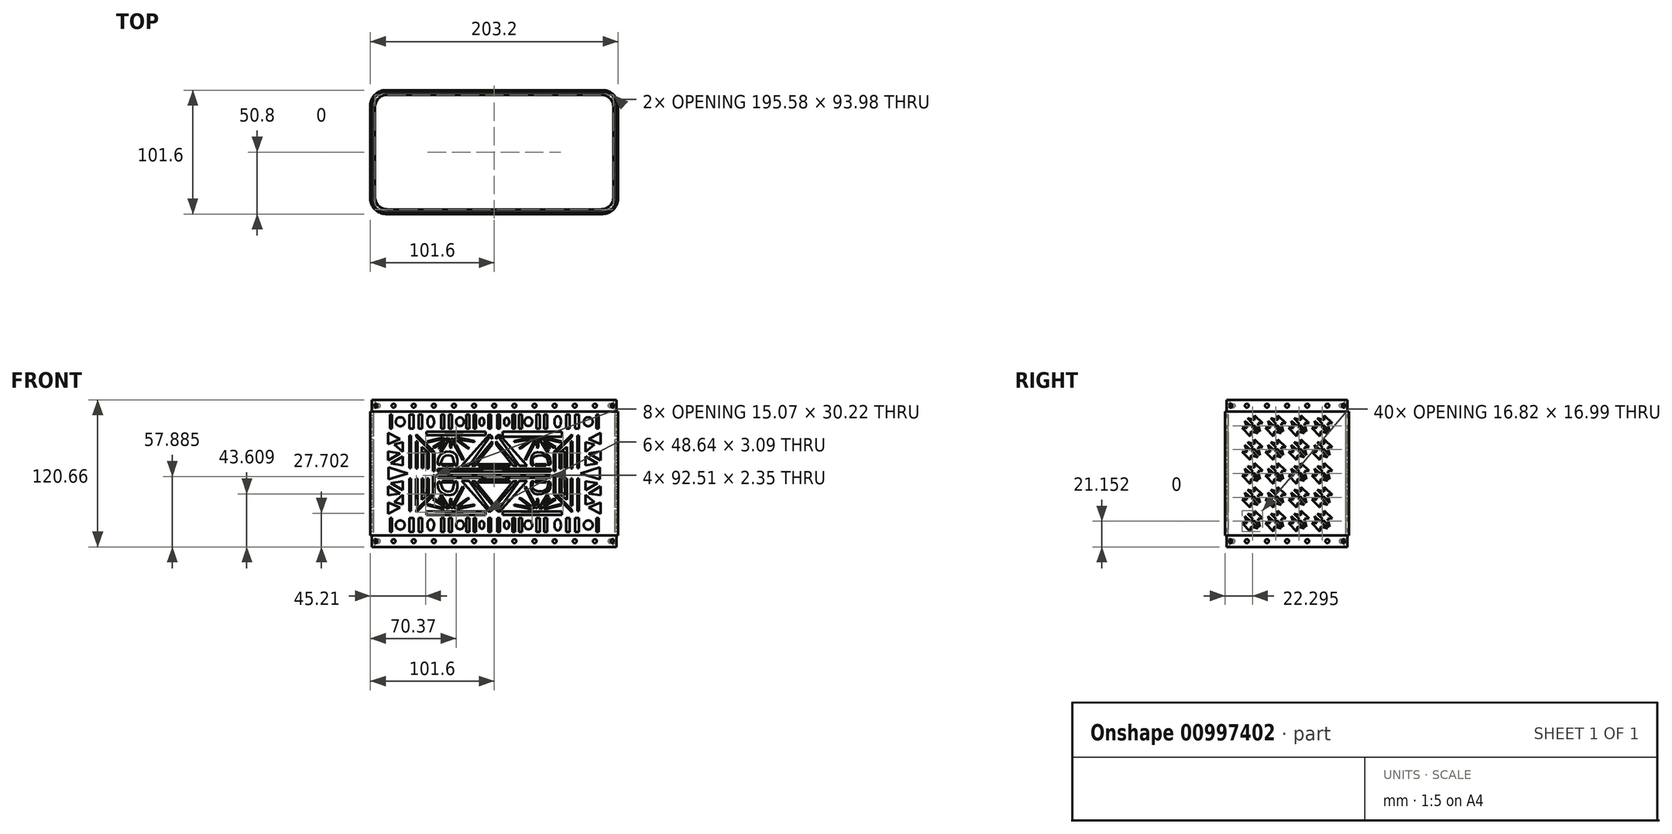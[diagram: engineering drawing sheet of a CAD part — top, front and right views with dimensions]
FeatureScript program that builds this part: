
annotation { "Feature Type Name" : "Feature", "Feature Type Description" : "" }
export const myFeature = defineFeature(function(context is Context, id is Id, definition is map)
    precondition{}
    {
        {
            var Q0;
            Q0=qCreatedBy(makeId("Top.planeOp"),FACE);
            var sketch = newSketch(context, id + "F0", { "sketchPlane" : qUnion([Q0])});
            skLineSegment(sketch, "E0.bottom", {"start": v(-88.9, 50.8) * mm, "end": v(88.9, 50.8) * mm});
            skLineSegment(sketch, "E0.top", {"start": v(-88.9, -50.8) * mm, "end": v(88.9, -50.8) * mm});
            skLineSegment(sketch, "E0.left", {"start": v(-101.6, 38.1) * mm, "end": v(-101.6, -38.1) * mm});
            skLineSegment(sketch, "E0.right", {"start": v(101.6, 38.1) * mm, "end": v(101.6, -38.1) * mm});
            skPoint(sketch, "E1.visualSharp", {"position": v(-101.6, -50.8) * mm});
            skArc(sketch, "E1.filletArc", {"start": v(-101.6, -38.1) * mm, "mid": v(-97.88, -47.08) * mm, "end": v(-88.9, -50.8) * mm});
            skPoint(sketch, "E2.visualSharp", {"position": v(101.6, -50.8) * mm});
            skArc(sketch, "E2.filletArc", {"start": v(88.9, -50.8) * mm, "mid": v(97.88, -47.08) * mm, "end": v(101.6, -38.1) * mm});
            skPoint(sketch, "E3.visualSharp", {"position": v(-101.6, 50.8) * mm});
            skArc(sketch, "E3.filletArc", {"start": v(-88.9, 50.8) * mm, "mid": v(-97.88, 47.08) * mm, "end": v(-101.6, 38.1) * mm});
            skPoint(sketch, "E4.visualSharp", {"position": v(101.6, 50.8) * mm});
            skArc(sketch, "E4.filletArc", {"start": v(101.6, 38.1) * mm, "mid": v(97.88, 47.08) * mm, "end": v(88.9, 50.8) * mm});
            skSolve(sketch);
        }
        {
            var Q0;
            Q0=makeQuery(id+"F0.imprint","IMPRINT",FACE,{"disambiguationData":[TD([[makeQuery(id+"F0.imprint","IMPRINT",EDGE,{"derivedFrom":sQuery(id+"F0.wireOp",EDGE,"E0.bottom")}),-1.0]])]});
            extrude(context, id + "F1", {"entities" : qUnion([Q0]), "depth" : 101.6 * mm, "offsetDistance" : 25.4 * mm});
        }
        {
            var Q0;
            Q0=makeQuery(id+"F1.opExtrude","CAP_FACE",FACE,{"disambiguationData":[OSD([sQuery(id+"F0.wireOp",EDGE,"E0.bottom"),sQuery(id+"F0.wireOp",EDGE,"E0.top"),sQuery(id+"F0.wireOp",EDGE,"E0.left"),sQuery(id+"F0.wireOp",EDGE,"E0.right"),sQuery(id+"F0.wireOp",EDGE,"E1.filletArc"),sQuery(id+"F0.wireOp",EDGE,"E2.filletArc"),sQuery(id+"F0.wireOp",EDGE,"E3.filletArc"),sQuery(id+"F0.wireOp",EDGE,"E4.filletArc")])],"isStart":false});
            var Q1;
            Q1=makeQuery(id+"F1.opExtrude","CAP_FACE",FACE,{"disambiguationData":[OSD([sQuery(id+"F0.wireOp",EDGE,"E0.bottom"),sQuery(id+"F0.wireOp",EDGE,"E0.top"),sQuery(id+"F0.wireOp",EDGE,"E0.left"),sQuery(id+"F0.wireOp",EDGE,"E0.right"),sQuery(id+"F0.wireOp",EDGE,"E1.filletArc"),sQuery(id+"F0.wireOp",EDGE,"E2.filletArc"),sQuery(id+"F0.wireOp",EDGE,"E3.filletArc"),sQuery(id+"F0.wireOp",EDGE,"E4.filletArc")])],"isStart":true});
            shell(context, id + "F2", {"entities" : qUnion([Q0, Q1]), "thickness" : 2.54 * mm});
        }
        {
            var Q0;
            Q0=makeQuery(id+"F1.opExtrude","CAP_FACE",FACE,{"disambiguationData":[OSD([sQuery(id+"F0.wireOp",EDGE,"E0.bottom"),sQuery(id+"F0.wireOp",EDGE,"E0.top"),sQuery(id+"F0.wireOp",EDGE,"E0.left"),sQuery(id+"F0.wireOp",EDGE,"E0.right"),sQuery(id+"F0.wireOp",EDGE,"E1.filletArc"),sQuery(id+"F0.wireOp",EDGE,"E2.filletArc"),sQuery(id+"F0.wireOp",EDGE,"E3.filletArc"),sQuery(id+"F0.wireOp",EDGE,"E4.filletArc")])],"isStart":false});
            var sketch = newSketch(context, id + "F3", { "sketchPlane" : qUnion([Q0])});
            skLineSegment(sketch, "E5.bottom", {"start": v(88.9, -49.53) * mm, "end": v(-88.9, -49.53) * mm});
            skLineSegment(sketch, "E5.top", {"start": v(88.9, 49.53) * mm, "end": v(-88.9, 49.53) * mm});
            skLineSegment(sketch, "E5.left", {"start": v(100.33, -38.1) * mm, "end": v(100.33, 38.1) * mm});
            skLineSegment(sketch, "E5.right", {"start": v(-100.33, -38.1) * mm, "end": v(-100.33, 38.1) * mm});
            skPoint(sketch, "E5.middle", {"position": v(0, 0) * mm});
            skPoint(sketch, "E6.visualSharp", {"position": v(-100.33, 49.53) * mm});
            skArc(sketch, "E6.filletArc", {"start": v(-88.9, 49.53) * mm, "mid": v(-96.98, 46.18) * mm, "end": v(-100.33, 38.1) * mm});
            skPoint(sketch, "E7.visualSharp", {"position": v(100.33, 49.53) * mm});
            skArc(sketch, "E7.filletArc", {"start": v(100.33, 38.1) * mm, "mid": v(96.98, 46.18) * mm, "end": v(88.9, 49.53) * mm});
            skPoint(sketch, "E8.visualSharp", {"position": v(100.33, -49.53) * mm});
            skArc(sketch, "E8.filletArc", {"start": v(88.9, -49.53) * mm, "mid": v(96.98, -46.18) * mm, "end": v(100.33, -38.1) * mm});
            skPoint(sketch, "E9.visualSharp", {"position": v(-100.33, -49.53) * mm});
            skArc(sketch, "E9.filletArc", {"start": v(-100.33, -38.1) * mm, "mid": v(-96.98, -46.18) * mm, "end": v(-88.9, -49.53) * mm});
            skLineSegment(sketch, "E10.bottom", {"start": v(-87.63, 46.99) * mm, "end": v(87.63, 47) * mm});
            skLineSegment(sketch, "E10.top", {"start": v(-87.63, -47) * mm, "end": v(87.63, -46.99) * mm});
            skLineSegment(sketch, "E10.left", {"start": v(-97.8, 36.83) * mm, "end": v(-97.8, -36.83) * mm});
            skLineSegment(sketch, "E10.right", {"start": v(97.8, 36.83) * mm, "end": v(97.8, -36.83) * mm});
            skPoint(sketch, "E11.visualSharp", {"position": v(-97.8, -47) * mm});
            skArc(sketch, "E11.filletArc", {"start": v(-97.8, -36.83) * mm, "mid": v(-94.81, -44.01) * mm, "end": v(-87.63, -47) * mm});
            skPoint(sketch, "E12.visualSharp", {"position": v(-97.8, 46.99) * mm});
            skArc(sketch, "E12.filletArc", {"start": v(-87.63, 47) * mm, "mid": v(-94.81, 44.01) * mm, "end": v(-97.8, 36.83) * mm});
            skPoint(sketch, "E13.visualSharp", {"position": v(97.8, 47) * mm});
            skArc(sketch, "E13.filletArc", {"start": v(97.8, 36.83) * mm, "mid": v(94.81, 44.01) * mm, "end": v(87.63, 47) * mm});
            skPoint(sketch, "E14.visualSharp", {"position": v(97.8, -46.99) * mm});
            skArc(sketch, "E14.filletArc", {"start": v(87.63, -46.99) * mm, "mid": v(94.81, -44.01) * mm, "end": v(97.8, -36.83) * mm});
            skSolve(sketch);
        }
        {
            var Q0;
            Q0=makeQuery(id+"F3.imprint","IMPRINT",FACE,{"disambiguationData":[TD([[makeQuery(id+"F3.imprint","IMPRINT",EDGE,{"derivedFrom":sQuery(id+"F3.wireOp",EDGE,"E10.bottom")}),1.0]])]});
            var Q1;
            Q1=makeQuery(id+"F3.imprint","IMPRINT",FACE,{"disambiguationData":[TD([[makeQuery(id+"F3.imprint","IMPRINT",EDGE,{"derivedFrom":sQuery(id+"F3.wireOp",EDGE,"E5.bottom")}),-1.0]])]});
            extrude(context, id + "F4", {"entities" : qUnion([Q0, Q1]), "operationType" : NewBodyOperationType.ADD, "depth" : 9.52 * mm, "offsetDistance" : 25.4 * mm});
        }
        {
            var Q0;
            Q0=qCreatedBy(makeId("Top.planeOp"),FACE);
            var sketch = newSketch(context, id + "F5", { "sketchPlane" : qUnion([Q0])});
            skLineSegment(sketch, "E15.bottom", {"start": v(-88.9, 49.53) * mm, "end": v(88.9, 49.53) * mm});
            skLineSegment(sketch, "E15.top", {"start": v(-88.9, -49.53) * mm, "end": v(88.9, -49.53) * mm});
            skLineSegment(sketch, "E15.left", {"start": v(-100.33, 38.1) * mm, "end": v(-100.33, -38.1) * mm});
            skLineSegment(sketch, "E15.right", {"start": v(100.33, 38.1) * mm, "end": v(100.33, -38.1) * mm});
            skPoint(sketch, "E15.middle", {"position": v(0, 0) * mm});
            skLineSegment(sketch, "E16.bottom", {"start": v(-87.63, -47) * mm, "end": v(87.63, -46.99) * mm});
            skLineSegment(sketch, "E16.top", {"start": v(-87.63, 46.99) * mm, "end": v(87.63, 47) * mm});
            skLineSegment(sketch, "E16.left", {"start": v(-97.8, -36.83) * mm, "end": v(-97.8, 36.83) * mm});
            skLineSegment(sketch, "E16.right", {"start": v(97.8, -36.83) * mm, "end": v(97.8, 36.83) * mm});
            skPoint(sketch, "E17.visualSharp", {"position": v(97.8, 47) * mm});
            skArc(sketch, "E17.filletArc", {"start": v(97.8, 36.83) * mm, "mid": v(94.81, 44.01) * mm, "end": v(87.63, 47) * mm});
            skPoint(sketch, "E18.visualSharp", {"position": v(-97.8, 46.99) * mm});
            skArc(sketch, "E18.filletArc", {"start": v(-87.63, 46.99) * mm, "mid": v(-94.81, 44.01) * mm, "end": v(-97.79, 36.83) * mm});
            skPoint(sketch, "E19.visualSharp", {"position": v(-97.8, -47) * mm});
            skArc(sketch, "E19.filletArc", {"start": v(-97.8, -36.83) * mm, "mid": v(-94.81, -44.01) * mm, "end": v(-87.63, -47) * mm});
            skPoint(sketch, "E20.visualSharp", {"position": v(97.8, -46.99) * mm});
            skArc(sketch, "E20.filletArc", {"start": v(87.63, -46.99) * mm, "mid": v(94.81, -44.01) * mm, "end": v(97.79, -36.83) * mm});
            skPoint(sketch, "E21.visualSharp", {"position": v(100.33, -49.53) * mm});
            skArc(sketch, "E21.filletArc", {"start": v(88.9, -49.53) * mm, "mid": v(96.98, -46.18) * mm, "end": v(100.33, -38.1) * mm});
            skPoint(sketch, "E22.visualSharp", {"position": v(-100.33, -49.53) * mm});
            skArc(sketch, "E22.filletArc", {"start": v(-100.33, -38.1) * mm, "mid": v(-96.98, -46.18) * mm, "end": v(-88.9, -49.53) * mm});
            skPoint(sketch, "E23.visualSharp", {"position": v(-100.33, 49.53) * mm});
            skArc(sketch, "E23.filletArc", {"start": v(-88.9, 49.53) * mm, "mid": v(-96.98, 46.18) * mm, "end": v(-100.33, 38.1) * mm});
            skPoint(sketch, "E24.visualSharp", {"position": v(100.33, 49.53) * mm});
            skArc(sketch, "E24.filletArc", {"start": v(100.33, 38.1) * mm, "mid": v(96.98, 46.18) * mm, "end": v(88.9, 49.53) * mm});
            skSolve(sketch);
        }
        {
            var Q0;
            Q0=qSketchRegion(id+"F5",true);
            extrude(context, id + "F6", {"entities" : qUnion([Q0]), "operationType" : NewBodyOperationType.ADD, "oppositeDirection" : true, "depth" : 9.52 * mm, "offsetDistance" : 25.4 * mm});
        }
        {
            var Q0;
            Q0=makeQuery(id+"F1.opExtrude","SWEPT_FACE",FACE,{"disambiguationData":[OSD([sQuery(id+"F0.wireOp",EDGE,"E0.top")])]});
            var sketch = newSketch(context, id + "F7", { "sketchPlane" : qUnion([Q0])});
            skPoint(sketch, "E25", {"position": v(-82.55, 50.8) * mm});
            skPoint(sketch, "E26", {"position": v(82.55, 50.8) * mm});
            skPoint(sketch, "E27", {"position": v(88.9, 50.8) * mm});
            skPoint(sketch, "E28", {"position": v(-88.9, 50.8) * mm});
            skPoint(sketch, "E29", {"position": v(0, 101.6) * mm});
            skPoint(sketch, "E30", {"position": v(0, 97.17) * mm});
            skSolve(sketch);
        }
        {
            var Q0;
            {var subQ0=sQuery(id+"F0.wireOp",EDGE,"E0.top");Q0=makeQuery(id+"F7.imprint","IMPRINT",FACE,{"disambiguationData":[TD([[makeQuery(id+"F7.imprint","IMPRINT",EDGE,{"derivedFrom":makeQuery(id+"F1.opExtrude","CAP_EDGE",EDGE,{"disambiguationData":[OSD([subQ0])],"isStart":true})}),1.0]])]});}
            var sketch = newSketch(context, id + "F8", { "sketchPlane" : qUnion([Q0])});
            skLineSegment(sketch, "E31.bottom", {"start": v(-69.54, 81.8) * mm, "end": v(-68.27, 81.8) * mm});
            skLineSegment(sketch, "E31.top", {"start": v(-69.54, 55.15) * mm, "end": v(-68.27, 55.15) * mm});
            skLineSegment(sketch, "E31.left", {"start": v(-69.54, 81.8) * mm, "end": v(-69.54, 55.15) * mm});
            skLineSegment(sketch, "E31.right", {"start": v(-68.27, 81.8) * mm, "end": v(-68.27, 55.15) * mm});
            skLineSegment(sketch, "E32.bottom", {"start": v(-64.12, 77.24) * mm, "end": v(-62.85, 77.24) * mm});
            skLineSegment(sketch, "E32.top", {"start": v(-64.12, 55) * mm, "end": v(-62.85, 55) * mm});
            skLineSegment(sketch, "E32.left", {"start": v(-64.12, 77.24) * mm, "end": v(-64.12, 55) * mm});
            skLineSegment(sketch, "E32.right", {"start": v(-62.85, 77.24) * mm, "end": v(-62.85, 55) * mm});
            skLineSegment(sketch, "E33", {"start": v(-59.53, 55.07) * mm, "end": v(-59.53, 72.59) * mm});
            skLineSegment(sketch, "E34", {"start": v(-59.53, 72.59) * mm, "end": v(-53.58, 67.88) * mm});
            skLineSegment(sketch, "E35", {"start": v(-53.58, 67.88) * mm, "end": v(-53.58, 55) * mm});
            skLineSegment(sketch, "E36", {"start": v(-53.58, 55) * mm, "end": v(-55.15, 55) * mm});
            skLineSegment(sketch, "E37", {"start": v(-55.15, 55) * mm, "end": v(-55.15, 66.64) * mm});
            skLineSegment(sketch, "E38", {"start": v(-55.15, 66.64) * mm, "end": v(-58.16, 68.8) * mm});
            skLineSegment(sketch, "E39", {"start": v(-59.53, 55.07) * mm, "end": v(-58.16, 55.07) * mm});
            skLineSegment(sketch, "E40", {"start": v(-58.16, 55.07) * mm, "end": v(-58.16, 68.8) * mm});
            skLineSegment(sketch, "E41", {"start": v(-50.14, 52.56) * mm, "end": v(-50.14, 67.28) * mm});
            skLineSegment(sketch, "E42", {"start": v(-50.14, 67.28) * mm, "end": v(-63.92, 80.98) * mm});
            skLineSegment(sketch, "E43", {"start": v(-63.92, 80.98) * mm, "end": v(-63.92, 82.78) * mm});
            skLineSegment(sketch, "E44", {"start": v(-63.92, 82.78) * mm, "end": v(-48.86, 68.23) * mm});
            skLineSegment(sketch, "E45", {"start": v(-48.86, 68.23) * mm, "end": v(-48.86, 52.56) * mm});
            skLineSegment(sketch, "E46", {"start": v(-48.86, 52.56) * mm, "end": v(-50.14, 52.56) * mm});
            skLineSegment(sketch, "E47.bottom", {"start": v(-55.55, 82.03) * mm, "end": v(-6.91, 82.03) * mm});
            skLineSegment(sketch, "E47.top", {"start": v(-55.55, 85.13) * mm, "end": v(-6.91, 85.13) * mm});
            skLineSegment(sketch, "E47.left", {"start": v(-55.55, 82.03) * mm, "end": v(-55.55, 85.13) * mm});
            skLineSegment(sketch, "E47.right", {"start": v(-6.91, 82.03) * mm, "end": v(-6.91, 85.13) * mm});
            skLineSegment(sketch, "E48", {"start": v(-55.1, 76.98) * mm, "end": v(-42.24, 80.13) * mm});
            skLineSegment(sketch, "E49", {"start": v(-42.24, 80.13) * mm, "end": v(-40.9, 79.45) * mm});
            skLineSegment(sketch, "E50", {"start": v(-40.9, 79.45) * mm, "end": v(-54.58, 76.07) * mm});
            skLineSegment(sketch, "E51", {"start": v(-54.58, 76.07) * mm, "end": v(-55.1, 76.98) * mm});
            skLineSegment(sketch, "E52", {"start": v(-50.33, 72.34) * mm, "end": v(-49.32, 71.33) * mm});
            skLineSegment(sketch, "E53", {"start": v(-49.32, 71.33) * mm, "end": v(-40.54, 77.24) * mm});
            skLineSegment(sketch, "E54", {"start": v(-40.54, 77.24) * mm, "end": v(-45.9, 71.84) * mm});
            skLineSegment(sketch, "E55", {"start": v(-45.9, 71.84) * mm, "end": v(-45.04, 70.98) * mm});
            skLineSegment(sketch, "E56", {"start": v(-45.04, 70.98) * mm, "end": v(-40.01, 76.03) * mm});
            skLineSegment(sketch, "E57", {"start": v(-40.01, 76.03) * mm, "end": v(-44.6, 68.93) * mm});
            skLineSegment(sketch, "E58", {"start": v(-44.6, 68.93) * mm, "end": v(-43.9, 67.87) * mm});
            skLineSegment(sketch, "E59", {"start": v(-43.9, 67.87) * mm, "end": v(-36.86, 79.28) * mm});
            skLineSegment(sketch, "E60", {"start": v(-36.86, 79.28) * mm, "end": v(-37.94, 79.94) * mm});
            skLineSegment(sketch, "E61", {"start": v(-37.94, 79.94) * mm, "end": v(-50.33, 72.34) * mm});
            skLineSegment(sketch, "E62", {"start": v(-36.28, 72.34) * mm, "end": v(-35.26, 71.33) * mm});
            skLineSegment(sketch, "E63", {"start": v(-34.02, 79.8) * mm, "end": v(-36.11, 78.38) * mm});
            skLineSegment(sketch, "E64", {"start": v(-36.11, 78.38) * mm, "end": v(-36.28, 72.34) * mm});
            skLineSegment(sketch, "E65", {"start": v(-34.02, 79.8) * mm, "end": v(-24.97, 62.28) * mm});
            skLineSegment(sketch, "E66", {"start": v(-24.97, 62.28) * mm, "end": v(-25.62, 61.62) * mm});
            skLineSegment(sketch, "E67", {"start": v(-22.03, 71.33) * mm, "end": v(-20.4, 71.33) * mm});
            skLineSegment(sketch, "E68", {"start": v(-20.4, 71.33) * mm, "end": v(-29.91, 78.67) * mm});
            skLineSegment(sketch, "E69", {"start": v(-29.91, 78.67) * mm, "end": v(-16.35, 76.46) * mm});
            skLineSegment(sketch, "E70", {"start": v(-16.35, 76.46) * mm, "end": v(-16.35, 77.5) * mm});
            skLineSegment(sketch, "E71", {"start": v(-16.35, 77.5) * mm, "end": v(-29.9, 80.27) * mm});
            skLineSegment(sketch, "E72", {"start": v(-29.9, 80.27) * mm, "end": v(-32.77, 79.37) * mm});
            skFitSpline(sketch, "E73", {"points": [v(-45.65, 57.64) * mm, v(-45.68, 63.84) * mm, v(-39.17, 68.5) * mm, v(-31.43, 66.27) * mm, v(-30.64, 57.48) * mm, v(-32.02, 57.42) * mm, v(-33.93, 63.5) * mm, v(-35.4, 65.37) * mm, v(-39.79, 65.41) * mm, v(-43.04, 61.77) * mm, v(-44.66, 57.59) * mm, v(-45.65, 57.64) * mm]});
            skLineSegment(sketch, "E74.bottom", {"start": v(-42.63, 58.33) * mm, "end": v(-33.5, 58.33) * mm});
            skLineSegment(sketch, "E74.top", {"start": v(-42.63, 57.12) * mm, "end": v(-33.5, 57.12) * mm});
            skLineSegment(sketch, "E74.left", {"start": v(-42.63, 58.33) * mm, "end": v(-42.63, 57.12) * mm});
            skLineSegment(sketch, "E74.right", {"start": v(-33.5, 58.33) * mm, "end": v(-33.5, 57.12) * mm});
            skLineSegment(sketch, "E75", {"start": v(-1.64, 77) * mm, "end": v(-1.64, 74.59) * mm});
            skLineSegment(sketch, "E76", {"start": v(-1.64, 74.59) * mm, "end": v(-15.46, 57.23) * mm});
            skLineSegment(sketch, "E77", {"start": v(-15.46, 57.23) * mm, "end": v(-18.54, 57.23) * mm});
            skLineSegment(sketch, "E78", {"start": v(-18.54, 57.23) * mm, "end": v(-1.64, 77) * mm});
            skLineSegment(sketch, "E79.bottom", {"start": v(-12.6, 58.38) * mm, "end": v(0, 58.38) * mm});
            skLineSegment(sketch, "E79.top", {"start": v(-12.6, 56.8) * mm, "end": v(0, 56.8) * mm});
            skLineSegment(sketch, "E79.left", {"start": v(-12.6, 58.38) * mm, "end": v(-12.6, 56.8) * mm});
            skLineSegment(sketch, "E79.right", {"start": v(0, 58.38) * mm, "end": v(0, 56.8) * mm});
            skLineSegment(sketch, "E80.bottom", {"start": v(-46.25, 54.57) * mm, "end": v(0, 54.57) * mm});
            skLineSegment(sketch, "E80.top", {"start": v(-46.25, 52.22) * mm, "end": v(0, 52.22) * mm});
            skLineSegment(sketch, "E80.left", {"start": v(-46.25, 54.57) * mm, "end": v(-46.25, 52.22) * mm});
            skLineSegment(sketch, "E80.right", {"start": v(0, 54.57) * mm, "end": v(0, 52.22) * mm});
            skLineSegment(sketch, "E81", {"start": v(-25.62, 61.62) * mm, "end": v(-34.64, 77.63) * mm});
            skLineSegment(sketch, "E82", {"start": v(-34.64, 77.63) * mm, "end": v(-35.26, 71.33) * mm});
            skLineSegment(sketch, "E83", {"start": v(-22.03, 71.33) * mm, "end": v(-32.77, 79.37) * mm});
            skLineSegment(sketch, "E84.MirrorCS", {"start": v(15.46, 57.23) * mm, "end": v(18.54, 57.23) * mm});
            skLineSegment(sketch, "E85.MirrorCS", {"start": v(1.64, 77) * mm, "end": v(1.64, 74.59) * mm});
            skLineSegment(sketch, "E86.MirrorCS", {"start": v(50.33, 72.34) * mm, "end": v(49.32, 71.33) * mm});
            skLineSegment(sketch, "E87.MirrorCS", {"start": v(36.86, 79.28) * mm, "end": v(37.94, 79.94) * mm});
            skLineSegment(sketch, "E88.MirrorCS", {"start": v(63.92, 80.98) * mm, "end": v(63.92, 82.78) * mm});
            skLineSegment(sketch, "E89.MirrorCS", {"start": v(45.9, 71.84) * mm, "end": v(45.04, 70.98) * mm});
            skLineSegment(sketch, "E90.MirrorCS", {"start": v(59.53, 55.07) * mm, "end": v(58.16, 55.07) * mm});
            skLineSegment(sketch, "E91.MirrorCS", {"start": v(55.55, 81.06) * mm, "end": v(55.55, 85.13) * mm});
            skLineSegment(sketch, "E92.MirrorCS", {"start": v(42.63, 58.33) * mm, "end": v(42.63, 57.12) * mm});
            skLineSegment(sketch, "E93.MirrorCS", {"start": v(36.28, 72.34) * mm, "end": v(35.26, 71.33) * mm});
            skLineSegment(sketch, "E94.MirrorCS", {"start": v(53.58, 55) * mm, "end": v(55.15, 55) * mm});
            skLineSegment(sketch, "E95.MirrorCS", {"start": v(29.9, 80.27) * mm, "end": v(32.77, 79.37) * mm});
            skLineSegment(sketch, "E96.MirrorCS", {"start": v(34.64, 77.63) * mm, "end": v(35.26, 71.33) * mm});
            skLineSegment(sketch, "E97.MirrorCS", {"start": v(64.12, 55) * mm, "end": v(62.85, 55) * mm});
            skLineSegment(sketch, "E98.MirrorCS", {"start": v(69.54, 55.15) * mm, "end": v(68.27, 55.15) * mm});
            skLineSegment(sketch, "E99.MirrorCS", {"start": v(33.5, 58.33) * mm, "end": v(33.5, 57.12) * mm});
            skLineSegment(sketch, "E100.MirrorCS", {"start": v(44.6, 68.93) * mm, "end": v(43.9, 67.87) * mm});
            skLineSegment(sketch, "E101.MirrorCS", {"start": v(54.58, 76.07) * mm, "end": v(55.1, 76.98) * mm});
            skLineSegment(sketch, "E102.MirrorCS", {"start": v(12.6, 58.38) * mm, "end": v(12.6, 56.8) * mm});
            skLineSegment(sketch, "E103.MirrorCS", {"start": v(24.97, 62.28) * mm, "end": v(25.62, 61.62) * mm});
            skLineSegment(sketch, "E104.MirrorCS", {"start": v(16.35, 76.46) * mm, "end": v(16.35, 77.5) * mm});
            skLineSegment(sketch, "E105.MirrorCS", {"start": v(6.91, 81.06) * mm, "end": v(6.91, 85.13) * mm});
            skLineSegment(sketch, "E106.MirrorCS", {"start": v(55.15, 66.64) * mm, "end": v(58.16, 68.8) * mm});
            skLineSegment(sketch, "E107.MirrorCS", {"start": v(45.04, 70.98) * mm, "end": v(40.01, 76.03) * mm});
            skLineSegment(sketch, "E108.MirrorCS", {"start": v(59.53, 72.59) * mm, "end": v(53.58, 67.88) * mm});
            skLineSegment(sketch, "E109.MirrorCS", {"start": v(64.12, 77.24) * mm, "end": v(62.85, 77.24) * mm});
            skLineSegment(sketch, "E110.MirrorCS", {"start": v(22.03, 71.33) * mm, "end": v(20.4, 71.33) * mm});
            skLineSegment(sketch, "E111.MirrorCS", {"start": v(36.11, 78.38) * mm, "end": v(36.28, 72.34) * mm});
            skLineSegment(sketch, "E112.MirrorCS", {"start": v(69.54, 81.8) * mm, "end": v(68.27, 81.8) * mm});
            skLineSegment(sketch, "E113.MirrorCS", {"start": v(34.02, 79.8) * mm, "end": v(36.11, 78.38) * mm});
            skLineSegment(sketch, "E114.MirrorCS", {"start": v(42.24, 80.13) * mm, "end": v(40.9, 79.45) * mm});
            skLineSegment(sketch, "E115.MirrorCS", {"start": v(46.25, 54.57) * mm, "end": v(46.25, 52.22) * mm});
            skLineSegment(sketch, "E116.MirrorCS", {"start": v(48.86, 52.56) * mm, "end": v(50.14, 52.56) * mm});
            skLineSegment(sketch, "E117.MirrorCS", {"start": v(49.32, 71.33) * mm, "end": v(40.54, 77.24) * mm});
            skLineSegment(sketch, "E118.MirrorCS", {"start": v(64.12, 77.24) * mm, "end": v(64.12, 55) * mm});
            skFitSpline(sketch, "E119.MirrorC", {"points": [v(45.65, 57.64) * mm, v(45.68, 63.84) * mm, v(38.4, 67.98) * mm, v(31.43, 66.27) * mm, v(30.64, 57.48) * mm, v(32.02, 57.42) * mm, v(31.25, 62.15) * mm, v(35.4, 65.37) * mm, v(39.79, 65.41) * mm, v(43.58, 62.94) * mm, v(44.66, 57.59) * mm, v(45.65, 57.64) * mm]});
            skLineSegment(sketch, "E120.MirrorCS", {"start": v(55.55, 81.06) * mm, "end": v(6.91, 81.06) * mm});
            skLineSegment(sketch, "E121.MirrorCS", {"start": v(40.9, 79.45) * mm, "end": v(54.58, 76.07) * mm});
            skLineSegment(sketch, "E122.MirrorCS", {"start": v(55.15, 55) * mm, "end": v(55.15, 66.64) * mm});
            skLineSegment(sketch, "E123.MirrorCS", {"start": v(58.16, 55.07) * mm, "end": v(58.16, 68.8) * mm});
            skLineSegment(sketch, "E124.MirrorCS", {"start": v(1.64, 74.59) * mm, "end": v(15.46, 57.23) * mm});
            skLineSegment(sketch, "E125.MirrorCS", {"start": v(55.55, 85.13) * mm, "end": v(6.91, 85.13) * mm});
            skLineSegment(sketch, "E126.MirrorCS", {"start": v(63.92, 82.78) * mm, "end": v(48.86, 68.23) * mm});
            skLineSegment(sketch, "E127.MirrorCS", {"start": v(34.02, 79.8) * mm, "end": v(24.97, 62.28) * mm});
            skLineSegment(sketch, "E128.MirrorCS", {"start": v(50.14, 67.28) * mm, "end": v(63.92, 80.98) * mm});
            skLineSegment(sketch, "E129.MirrorCS", {"start": v(18.54, 57.23) * mm, "end": v(1.64, 77) * mm});
            skLineSegment(sketch, "E130.MirrorCS", {"start": v(12.6, 58.38) * mm, "end": v(0, 58.38) * mm});
            skLineSegment(sketch, "E131.MirrorCS", {"start": v(59.53, 55.07) * mm, "end": v(59.53, 72.59) * mm});
            skLineSegment(sketch, "E132.MirrorCS", {"start": v(68.27, 81.8) * mm, "end": v(68.27, 55.15) * mm});
            skLineSegment(sketch, "E133.MirrorCS", {"start": v(40.54, 77.24) * mm, "end": v(45.9, 71.84) * mm});
            skLineSegment(sketch, "E134.MirrorCS", {"start": v(62.85, 77.24) * mm, "end": v(62.85, 55) * mm});
            skLineSegment(sketch, "E135.MirrorCS", {"start": v(46.25, 54.57) * mm, "end": v(0, 54.57) * mm});
            skLineSegment(sketch, "E136.MirrorCS", {"start": v(42.63, 58.33) * mm, "end": v(33.5, 58.33) * mm});
            skLineSegment(sketch, "E137.MirrorCS", {"start": v(16.35, 77.5) * mm, "end": v(29.9, 80.27) * mm});
            skLineSegment(sketch, "E138.MirrorCS", {"start": v(29.91, 78.67) * mm, "end": v(16.35, 76.46) * mm});
            skLineSegment(sketch, "E139.MirrorCS", {"start": v(12.6, 56.8) * mm, "end": v(0, 56.8) * mm});
            skLineSegment(sketch, "E140.MirrorCS", {"start": v(40.01, 76.03) * mm, "end": v(44.6, 68.93) * mm});
            skLineSegment(sketch, "E141.MirrorCS", {"start": v(25.62, 61.62) * mm, "end": v(34.64, 77.63) * mm});
            skLineSegment(sketch, "E142.MirrorCS", {"start": v(43.9, 67.87) * mm, "end": v(36.86, 79.28) * mm});
            skLineSegment(sketch, "E143.MirrorCS", {"start": v(46.25, 52.22) * mm, "end": v(0, 52.22) * mm});
            skLineSegment(sketch, "E144.MirrorCS", {"start": v(42.63, 57.12) * mm, "end": v(33.5, 57.12) * mm});
            skLineSegment(sketch, "E145.MirrorCS", {"start": v(69.54, 81.8) * mm, "end": v(69.54, 55.15) * mm});
            skLineSegment(sketch, "E146.MirrorCS", {"start": v(48.86, 68.23) * mm, "end": v(48.86, 52.56) * mm});
            skLineSegment(sketch, "E147.MirrorCS", {"start": v(50.14, 52.56) * mm, "end": v(50.14, 67.28) * mm});
            skLineSegment(sketch, "E148.MirrorCS", {"start": v(55.1, 76.98) * mm, "end": v(42.24, 80.13) * mm});
            skLineSegment(sketch, "E149.MirrorCS", {"start": v(37.94, 79.94) * mm, "end": v(50.33, 72.34) * mm});
            skLineSegment(sketch, "E150.MirrorCS", {"start": v(22.03, 71.33) * mm, "end": v(32.77, 79.37) * mm});
            skLineSegment(sketch, "E151.MirrorCS", {"start": v(53.58, 67.88) * mm, "end": v(53.58, 55) * mm});
            skLineSegment(sketch, "E152.MirrorCS", {"start": v(20.4, 71.33) * mm, "end": v(29.91, 78.67) * mm});
            skLineSegment(sketch, "E153", {"start": v(0, 50.88) * mm, "end": v(-88.8, 50.88) * mm, "construction": true});
            skLineSegment(sketch, "E154.MirrorCS", {"start": v(-12.6, 44.95) * mm, "end": v(0, 44.95) * mm});
            skLineSegment(sketch, "E155.MirrorCS", {"start": v(-12.6, 43.38) * mm, "end": v(0, 43.38) * mm});
            skLineSegment(sketch, "E156.MirrorCS", {"start": v(-1.64, 27.17) * mm, "end": v(-15.46, 44.52) * mm});
            skLineSegment(sketch, "E157.MirrorCS", {"start": v(-18.54, 44.52) * mm, "end": v(-1.64, 24.76) * mm});
            skLineSegment(sketch, "E158.MirrorCS", {"start": v(-46.25, 49.53) * mm, "end": v(0, 49.53) * mm});
            skLineSegment(sketch, "E159.MirrorCS", {"start": v(-46.25, 47.18) * mm, "end": v(0, 47.18) * mm});
            skLineSegment(sketch, "E160.MirrorCS", {"start": v(-46.25, 47.18) * mm, "end": v(-46.25, 49.53) * mm});
            skLineSegment(sketch, "E161.MirrorCS", {"start": v(-48.86, 49.19) * mm, "end": v(-50.14, 49.19) * mm});
            skLineSegment(sketch, "E162.MirrorCS", {"start": v(-48.86, 33.53) * mm, "end": v(-48.86, 49.19) * mm});
            skLineSegment(sketch, "E163.MirrorCS", {"start": v(-50.14, 49.19) * mm, "end": v(-50.14, 34.47) * mm});
            skLineSegment(sketch, "E164.MirrorCS", {"start": v(-53.58, 46.75) * mm, "end": v(-55.15, 46.75) * mm});
            skLineSegment(sketch, "E165.MirrorCS", {"start": v(-55.15, 46.75) * mm, "end": v(-55.15, 35.11) * mm});
            skLineSegment(sketch, "E166.MirrorCS", {"start": v(-53.58, 33.87) * mm, "end": v(-53.58, 46.75) * mm});
            skLineSegment(sketch, "E167.MirrorCS", {"start": v(-58.16, 46.68) * mm, "end": v(-58.16, 32.95) * mm});
            skLineSegment(sketch, "E168.MirrorCS", {"start": v(-59.53, 46.68) * mm, "end": v(-58.16, 46.68) * mm});
            skLineSegment(sketch, "E169.MirrorCS", {"start": v(-59.53, 46.68) * mm, "end": v(-59.53, 29.16) * mm});
            skLineSegment(sketch, "E170.MirrorCS", {"start": v(-62.85, 24.52) * mm, "end": v(-62.85, 46.76) * mm});
            skLineSegment(sketch, "E171.MirrorCS", {"start": v(-64.12, 24.52) * mm, "end": v(-64.12, 46.76) * mm});
            skLineSegment(sketch, "E172.MirrorCS", {"start": v(-64.12, 46.76) * mm, "end": v(-62.85, 46.76) * mm});
            skLineSegment(sketch, "E173.MirrorCS", {"start": v(-69.54, 46.6) * mm, "end": v(-68.27, 46.6) * mm});
            skLineSegment(sketch, "E174.MirrorCS", {"start": v(-69.54, 19.94) * mm, "end": v(-69.54, 46.6) * mm});
            skLineSegment(sketch, "E175.MirrorCS", {"start": v(-68.27, 19.94) * mm, "end": v(-68.27, 46.6) * mm});
            skLineSegment(sketch, "E176.MirrorCS", {"start": v(-34.02, 21.96) * mm, "end": v(-36.11, 23.37) * mm});
            skLineSegment(sketch, "E177.MirrorCS", {"start": v(-29.9, 21.48) * mm, "end": v(-32.77, 22.38) * mm});
            skLineSegment(sketch, "E178.MirrorCS", {"start": v(-50.33, 29.41) * mm, "end": v(-49.32, 30.42) * mm});
            skLineSegment(sketch, "E179.MirrorCS", {"start": v(-55.55, 19.72) * mm, "end": v(-55.55, 16.63) * mm});
            skLineSegment(sketch, "E180.MirrorCS", {"start": v(-16.35, 25.3) * mm, "end": v(-16.35, 24.25) * mm});
            skLineSegment(sketch, "E181.MirrorCS", {"start": v(-22.03, 30.42) * mm, "end": v(-20.4, 30.42) * mm});
            skLineSegment(sketch, "E182.MirrorCS", {"start": v(-24.97, 39.48) * mm, "end": v(-25.62, 40.13) * mm});
            skLineSegment(sketch, "E183.MirrorCS", {"start": v(-69.54, 19.94) * mm, "end": v(-68.27, 19.94) * mm});
            skLineSegment(sketch, "E184.MirrorCS", {"start": v(-63.92, 20.77) * mm, "end": v(-63.92, 18.97) * mm});
            skLineSegment(sketch, "E185.MirrorCS", {"start": v(-33.5, 43.42) * mm, "end": v(-33.5, 44.63) * mm});
            skLineSegment(sketch, "E186.MirrorCS", {"start": v(-15.46, 44.52) * mm, "end": v(-18.54, 44.52) * mm});
            skLineSegment(sketch, "E187.MirrorCS", {"start": v(-6.91, 19.72) * mm, "end": v(-6.91, 16.63) * mm});
            skLineSegment(sketch, "E188.MirrorCS", {"start": v(-55.15, 35.11) * mm, "end": v(-58.16, 32.95) * mm});
            skLineSegment(sketch, "E189.MirrorCS", {"start": v(-44.6, 32.83) * mm, "end": v(-43.9, 33.88) * mm});
            skLineSegment(sketch, "E190.MirrorCS", {"start": v(-42.24, 21.62) * mm, "end": v(-40.9, 22.3) * mm});
            skLineSegment(sketch, "E191.MirrorCS", {"start": v(-36.28, 29.41) * mm, "end": v(-35.26, 30.42) * mm});
            skLineSegment(sketch, "E192.MirrorCS", {"start": v(-45.9, 29.92) * mm, "end": v(-45.04, 30.78) * mm});
            skLineSegment(sketch, "E193.MirrorCS", {"start": v(-64.12, 24.52) * mm, "end": v(-62.85, 24.52) * mm});
            skLineSegment(sketch, "E194.MirrorCS", {"start": v(-12.6, 43.38) * mm, "end": v(-12.6, 44.95) * mm});
            skLineSegment(sketch, "E195.MirrorCS", {"start": v(-54.58, 25.68) * mm, "end": v(-55.1, 24.77) * mm});
            skLineSegment(sketch, "E196.MirrorCS", {"start": v(-36.86, 22.48) * mm, "end": v(-37.94, 21.81) * mm});
            skLineSegment(sketch, "E197.MirrorCS", {"start": v(-42.63, 43.42) * mm, "end": v(-42.63, 44.63) * mm});
            skLineSegment(sketch, "E198.MirrorCS", {"start": v(-40.01, 25.72) * mm, "end": v(-44.6, 32.83) * mm});
            skLineSegment(sketch, "E199.MirrorCS", {"start": v(-36.11, 23.37) * mm, "end": v(-36.28, 29.41) * mm});
            skFitSpline(sketch, "E200.MirrorC", {"points": [v(-45.65, 44.1) * mm, v(-45.68, 37.91) * mm, v(-39.17, 33.24) * mm, v(-31.43, 35.48) * mm, v(-30.64, 44.27) * mm, v(-32.02, 44.33) * mm, v(-33.93, 38.25) * mm, v(-35.4, 36.38) * mm, v(-39.79, 36.34) * mm, v(-43.04, 39.98) * mm, v(-44.66, 44.16) * mm, v(-45.65, 44.1) * mm]});
            skLineSegment(sketch, "E201.MirrorCS", {"start": v(-40.54, 24.52) * mm, "end": v(-45.9, 29.92) * mm});
            skLineSegment(sketch, "E202.MirrorCS", {"start": v(-34.64, 24.12) * mm, "end": v(-35.26, 30.42) * mm});
            skLineSegment(sketch, "E203.MirrorCS", {"start": v(-29.91, 23.08) * mm, "end": v(-16.35, 25.3) * mm});
            skLineSegment(sketch, "E204.MirrorCS", {"start": v(-16.35, 24.25) * mm, "end": v(-29.9, 21.48) * mm});
            skLineSegment(sketch, "E205.MirrorCS", {"start": v(-55.55, 19.72) * mm, "end": v(-6.91, 19.72) * mm});
            skLineSegment(sketch, "E206.MirrorCS", {"start": v(-25.62, 40.13) * mm, "end": v(-34.64, 24.12) * mm});
            skLineSegment(sketch, "E207.MirrorCS", {"start": v(-59.53, 29.16) * mm, "end": v(-53.58, 33.87) * mm});
            skLineSegment(sketch, "E208.MirrorCS", {"start": v(-42.63, 43.42) * mm, "end": v(-33.5, 43.42) * mm});
            skLineSegment(sketch, "E209.MirrorCS", {"start": v(-43.9, 33.88) * mm, "end": v(-36.86, 22.48) * mm});
            skLineSegment(sketch, "E210.MirrorCS", {"start": v(-1.64, 24.76) * mm, "end": v(-1.64, 27.17) * mm});
            skLineSegment(sketch, "E211.MirrorCS", {"start": v(-50.14, 34.47) * mm, "end": v(-63.92, 20.77) * mm});
            skLineSegment(sketch, "E212.MirrorCS", {"start": v(-55.1, 24.77) * mm, "end": v(-42.24, 21.62) * mm});
            skLineSegment(sketch, "E213.MirrorCS", {"start": v(-34.02, 21.96) * mm, "end": v(-24.97, 39.48) * mm});
            skLineSegment(sketch, "E214.MirrorCS", {"start": v(-63.92, 18.97) * mm, "end": v(-48.86, 33.53) * mm});
            skLineSegment(sketch, "E215.MirrorCS", {"start": v(-40.9, 22.3) * mm, "end": v(-54.58, 25.68) * mm});
            skLineSegment(sketch, "E216.MirrorCS", {"start": v(-42.63, 44.63) * mm, "end": v(-33.5, 44.63) * mm});
            skLineSegment(sketch, "E217.MirrorCS", {"start": v(-37.94, 21.81) * mm, "end": v(-50.33, 29.41) * mm});
            skLineSegment(sketch, "E218.MirrorCS", {"start": v(-55.55, 16.63) * mm, "end": v(-6.91, 16.63) * mm});
            skLineSegment(sketch, "E219.MirrorCS", {"start": v(-20.4, 30.42) * mm, "end": v(-29.91, 23.08) * mm});
            skLineSegment(sketch, "E220.MirrorCS", {"start": v(-49.32, 30.42) * mm, "end": v(-40.54, 24.52) * mm});
            skLineSegment(sketch, "E221.MirrorCS", {"start": v(-22.03, 30.42) * mm, "end": v(-32.77, 22.38) * mm});
            skLineSegment(sketch, "E222.MirrorCS", {"start": v(-45.04, 30.78) * mm, "end": v(-40.01, 25.72) * mm});
            skLineSegment(sketch, "E223.MirrorCS", {"start": v(1.64, 24.76) * mm, "end": v(1.64, 27.17) * mm});
            skLineSegment(sketch, "E224.MirrorCS", {"start": v(42.63, 43.42) * mm, "end": v(42.63, 44.63) * mm});
            skLineSegment(sketch, "E225.MirrorCS", {"start": v(46.25, 47.18) * mm, "end": v(46.25, 49.53) * mm});
            skLineSegment(sketch, "E226.MirrorCS", {"start": v(33.5, 43.42) * mm, "end": v(33.5, 44.63) * mm});
            skLineSegment(sketch, "E227.MirrorCS", {"start": v(64.12, 46.76) * mm, "end": v(62.85, 46.76) * mm});
            skLineSegment(sketch, "E228.MirrorCS", {"start": v(64.12, 24.52) * mm, "end": v(62.85, 24.52) * mm});
            skLineSegment(sketch, "E229.MirrorCS", {"start": v(34.02, 21.96) * mm, "end": v(36.11, 23.37) * mm});
            skLineSegment(sketch, "E230.MirrorCS", {"start": v(24.97, 39.48) * mm, "end": v(25.62, 40.13) * mm});
            skLineSegment(sketch, "E231.MirrorCS", {"start": v(42.24, 21.62) * mm, "end": v(40.9, 22.3) * mm});
            skLineSegment(sketch, "E232.MirrorCS", {"start": v(12.6, 43.38) * mm, "end": v(12.6, 44.95) * mm});
            skLineSegment(sketch, "E233.MirrorCS", {"start": v(36.28, 29.41) * mm, "end": v(35.26, 30.42) * mm});
            skLineSegment(sketch, "E234.MirrorCS", {"start": v(50.33, 29.41) * mm, "end": v(49.32, 30.42) * mm});
            skLineSegment(sketch, "E235.MirrorCS", {"start": v(69.54, 46.6) * mm, "end": v(68.27, 46.6) * mm});
            skLineSegment(sketch, "E236.MirrorCS", {"start": v(44.6, 32.83) * mm, "end": v(43.9, 33.88) * mm});
            skLineSegment(sketch, "E237.MirrorCS", {"start": v(16.35, 25.3) * mm, "end": v(16.35, 24.25) * mm});
            skLineSegment(sketch, "E238.MirrorCS", {"start": v(55.15, 35.11) * mm, "end": v(58.16, 32.95) * mm});
            skLineSegment(sketch, "E239.MirrorCS", {"start": v(54.58, 25.68) * mm, "end": v(55.1, 24.77) * mm});
            skLineSegment(sketch, "E240.MirrorCS", {"start": v(45.9, 29.92) * mm, "end": v(45.04, 30.78) * mm});
            skLineSegment(sketch, "E241.MirrorCS", {"start": v(59.53, 46.68) * mm, "end": v(58.16, 46.68) * mm});
            skLineSegment(sketch, "E242.MirrorCS", {"start": v(69.54, 19.94) * mm, "end": v(68.27, 19.94) * mm});
            skLineSegment(sketch, "E243.MirrorCS", {"start": v(15.46, 44.52) * mm, "end": v(18.54, 44.52) * mm});
            skLineSegment(sketch, "E244.MirrorCS", {"start": v(29.9, 21.48) * mm, "end": v(32.77, 22.38) * mm});
            skLineSegment(sketch, "E245.MirrorCS", {"start": v(63.92, 20.77) * mm, "end": v(63.92, 18.97) * mm});
            skLineSegment(sketch, "E246.MirrorCS", {"start": v(53.58, 46.75) * mm, "end": v(55.15, 46.75) * mm});
            skLineSegment(sketch, "E247.MirrorCS", {"start": v(36.86, 22.48) * mm, "end": v(37.94, 21.81) * mm});
            skLineSegment(sketch, "E248.MirrorCS", {"start": v(22.03, 30.42) * mm, "end": v(20.4, 30.42) * mm});
            skLineSegment(sketch, "E249.MirrorCS", {"start": v(58.16, 46.68) * mm, "end": v(58.16, 32.95) * mm});
            skLineSegment(sketch, "E250.MirrorCS", {"start": v(22.03, 30.42) * mm, "end": v(32.77, 22.38) * mm});
            skLineSegment(sketch, "E251.MirrorCS", {"start": v(42.63, 44.63) * mm, "end": v(33.5, 44.63) * mm});
            skLineSegment(sketch, "E252.MirrorCS", {"start": v(40.01, 25.72) * mm, "end": v(44.6, 32.83) * mm});
            skLineSegment(sketch, "E253.MirrorCS", {"start": v(53.58, 33.87) * mm, "end": v(53.58, 46.75) * mm});
            skLineSegment(sketch, "E254.MirrorCS", {"start": v(16.35, 24.25) * mm, "end": v(29.9, 21.48) * mm});
            skLineSegment(sketch, "E255.MirrorCS", {"start": v(40.9, 22.3) * mm, "end": v(54.58, 25.68) * mm});
            skLineSegment(sketch, "E256.MirrorCS", {"start": v(20.4, 30.42) * mm, "end": v(29.91, 23.08) * mm});
            skLineSegment(sketch, "E257.MirrorCS", {"start": v(42.63, 43.42) * mm, "end": v(33.5, 43.42) * mm});
            skLineSegment(sketch, "E258.MirrorCS", {"start": v(29.91, 23.08) * mm, "end": v(16.35, 25.3) * mm});
            skLineSegment(sketch, "E259.MirrorCS", {"start": v(46.25, 49.53) * mm, "end": v(0, 49.53) * mm});
            skLineSegment(sketch, "E260.MirrorCS", {"start": v(55.15, 46.75) * mm, "end": v(55.15, 35.11) * mm});
            skLineSegment(sketch, "E261.MirrorCS", {"start": v(69.54, 19.94) * mm, "end": v(69.54, 46.6) * mm});
            skLineSegment(sketch, "E262.MirrorCS", {"start": v(25.62, 40.13) * mm, "end": v(34.64, 24.12) * mm});
            skLineSegment(sketch, "E263.MirrorCS", {"start": v(40.54, 24.52) * mm, "end": v(45.9, 29.92) * mm});
            skLineSegment(sketch, "E264.MirrorCS", {"start": v(55.55, 19.7) * mm, "end": v(6.91, 19.7) * mm});
            skLineSegment(sketch, "E265.MirrorCS", {"start": v(49.32, 30.42) * mm, "end": v(40.54, 24.52) * mm});
            skLineSegment(sketch, "E266.MirrorCS", {"start": v(37.94, 21.81) * mm, "end": v(50.33, 29.41) * mm});
            skLineSegment(sketch, "E267.MirrorCS", {"start": v(63.92, 18.97) * mm, "end": v(48.86, 33.53) * mm});
            skLineSegment(sketch, "E268.MirrorCS", {"start": v(64.12, 24.52) * mm, "end": v(64.12, 46.76) * mm});
            skLineSegment(sketch, "E269.MirrorCS", {"start": v(59.53, 29.16) * mm, "end": v(53.58, 33.87) * mm});
            skLineSegment(sketch, "E270.MirrorCS", {"start": v(48.86, 49.19) * mm, "end": v(50.14, 49.19) * mm});
            skLineSegment(sketch, "E271.MirrorCS", {"start": v(12.6, 44.95) * mm, "end": v(0, 44.95) * mm});
            skLineSegment(sketch, "E272.MirrorCS", {"start": v(55.1, 24.77) * mm, "end": v(42.24, 21.62) * mm});
            skLineSegment(sketch, "E273.MirrorCS", {"start": v(1.64, 27.17) * mm, "end": v(15.46, 44.52) * mm});
            skLineSegment(sketch, "E274.MirrorCS", {"start": v(12.6, 43.38) * mm, "end": v(0, 43.38) * mm});
            skLineSegment(sketch, "E275.MirrorCS", {"start": v(46.25, 47.18) * mm, "end": v(0, 47.18) * mm});
            skLineSegment(sketch, "E276.MirrorCS", {"start": v(68.27, 19.94) * mm, "end": v(68.27, 46.6) * mm});
            skLineSegment(sketch, "E277.MirrorCS", {"start": v(59.53, 46.68) * mm, "end": v(59.53, 29.16) * mm});
            skLineSegment(sketch, "E278.MirrorCS", {"start": v(43.9, 33.88) * mm, "end": v(36.86, 22.48) * mm});
            skLineSegment(sketch, "E279.MirrorCS", {"start": v(48.86, 33.53) * mm, "end": v(48.86, 49.19) * mm});
            skLineSegment(sketch, "E280.MirrorCS", {"start": v(36.11, 23.37) * mm, "end": v(36.28, 29.41) * mm});
            skLineSegment(sketch, "E281.MirrorCS", {"start": v(62.85, 24.52) * mm, "end": v(62.85, 46.76) * mm});
            skFitSpline(sketch, "E282.MirrorC", {"points": [v(45.65, 44.1) * mm, v(45.68, 37.91) * mm, v(38.4, 33.78) * mm, v(31.43, 35.48) * mm, v(30.64, 44.27) * mm, v(32.02, 44.33) * mm, v(31.25, 39.6) * mm, v(35.4, 36.38) * mm, v(39.79, 36.34) * mm, v(43.58, 38.81) * mm, v(44.66, 44.16) * mm, v(45.65, 44.1) * mm]});
            skLineSegment(sketch, "E283.MirrorCS", {"start": v(18.54, 44.52) * mm, "end": v(1.64, 24.76) * mm});
            skLineSegment(sketch, "E284.MirrorCS", {"start": v(45.04, 30.78) * mm, "end": v(40.01, 25.72) * mm});
            skLineSegment(sketch, "E285.MirrorCS", {"start": v(50.14, 49.19) * mm, "end": v(50.14, 34.47) * mm});
            skLineSegment(sketch, "E286.MirrorCS", {"start": v(34.64, 24.12) * mm, "end": v(35.26, 30.42) * mm});
            skLineSegment(sketch, "E287.MirrorCS", {"start": v(50.14, 34.47) * mm, "end": v(63.92, 20.77) * mm});
            skLineSegment(sketch, "E288.MirrorCS", {"start": v(34.02, 21.96) * mm, "end": v(24.97, 39.48) * mm});
            skLineSegment(sketch, "E289", {"start": v(-26.87, 57.1) * mm, "end": v(-20.6, 57.1) * mm});
            skLineSegment(sketch, "E290", {"start": v(-20.6, 57.1) * mm, "end": v(-3.48, 80.9) * mm});
            skLineSegment(sketch, "E291", {"start": v(-3.48, 80.9) * mm, "end": v(-1.52, 78.93) * mm});
            skLineSegment(sketch, "E292", {"start": v(-1.52, 78.93) * mm, "end": v(-1.52, 80.9) * mm});
            skLineSegment(sketch, "E293", {"start": v(-1.52, 80.9) * mm, "end": v(-3.97, 82.86) * mm});
            skLineSegment(sketch, "E294", {"start": v(-3.97, 82.86) * mm, "end": v(-26.87, 57.1) * mm});
            skLineSegment(sketch, "E295.MirrorCS", {"start": v(1.52, 78.93) * mm, "end": v(1.52, 80.9) * mm});
            skLineSegment(sketch, "E296.MirrorCS", {"start": v(1.52, 80.9) * mm, "end": v(3.97, 82.86) * mm});
            skLineSegment(sketch, "E297.MirrorCS", {"start": v(3.48, 80.9) * mm, "end": v(1.52, 78.93) * mm});
            skLineSegment(sketch, "E298.MirrorCS", {"start": v(20.6, 57.1) * mm, "end": v(3.48, 80.9) * mm});
            skLineSegment(sketch, "E299.MirrorCS", {"start": v(26.87, 57.1) * mm, "end": v(20.6, 57.1) * mm});
            skLineSegment(sketch, "E300.MirrorCS", {"start": v(3.97, 82.86) * mm, "end": v(26.87, 57.1) * mm});
            skLineSegment(sketch, "E301.MirrorCS", {"start": v(1.52, 20.86) * mm, "end": v(3.97, 18.9) * mm});
            skLineSegment(sketch, "E302.MirrorCS", {"start": v(26.87, 44.66) * mm, "end": v(20.6, 44.66) * mm});
            skLineSegment(sketch, "E303.MirrorCS", {"start": v(20.6, 44.66) * mm, "end": v(3.48, 20.86) * mm});
            skLineSegment(sketch, "E304.MirrorCS", {"start": v(3.97, 18.9) * mm, "end": v(26.87, 44.66) * mm});
            skLineSegment(sketch, "E305.MirrorCS", {"start": v(3.48, 20.86) * mm, "end": v(1.52, 22.82) * mm});
            skLineSegment(sketch, "E306.MirrorCS", {"start": v(1.52, 22.82) * mm, "end": v(1.52, 20.86) * mm});
            skLineSegment(sketch, "E307.MirrorCS", {"start": v(-3.48, 20.86) * mm, "end": v(-1.52, 22.82) * mm});
            skLineSegment(sketch, "E308.MirrorCS", {"start": v(-1.52, 22.82) * mm, "end": v(-1.52, 20.86) * mm});
            skLineSegment(sketch, "E309.MirrorCS", {"start": v(-1.52, 20.86) * mm, "end": v(-3.97, 18.9) * mm});
            skLineSegment(sketch, "E310.MirrorCS", {"start": v(-26.87, 44.66) * mm, "end": v(-20.6, 44.66) * mm});
            skLineSegment(sketch, "E311.MirrorCS", {"start": v(-20.6, 44.66) * mm, "end": v(-3.48, 20.86) * mm});
            skLineSegment(sketch, "E312.MirrorCS", {"start": v(-3.97, 18.9) * mm, "end": v(-26.87, 44.66) * mm});
            skLineSegment(sketch, "E313", {"start": v(0, 102) * mm, "end": v(0, 0) * mm, "construction": true});
            skLineSegment(sketch, "E314", {"start": v(-88.8, 8.52) * mm, "end": v(0, 8.52) * mm, "construction": true});
            skLineSegment(sketch, "E315.bottom", {"start": v(-83.9, 14.14) * mm, "end": v(-85.54, 14.14) * mm});
            skLineSegment(sketch, "E315.top", {"start": v(-83.9, 2.9) * mm, "end": v(-85.54, 2.9) * mm});
            skLineSegment(sketch, "E315.left", {"start": v(-83.9, 14.14) * mm, "end": v(-83.9, 2.9) * mm});
            skLineSegment(sketch, "E315.right", {"start": v(-85.54, 14.14) * mm, "end": v(-85.54, 2.9) * mm});
            skPoint(sketch, "E315.middle", {"position": v(-84.73, 8.52) * mm});
            skCircle(sketch, "E316", {"center": v(-77.1, 8.52) * mm, "radius": 3.7 * mm});
            skLineSegment(sketch, "E317.bottom", {"start": v(-69.48, 14.14) * mm, "end": v(-66.22, 14.14) * mm});
            skLineSegment(sketch, "E317.top", {"start": v(-69.48, 2.9) * mm, "end": v(-66.22, 2.9) * mm});
            skLineSegment(sketch, "E317.left", {"start": v(-69.48, 14.14) * mm, "end": v(-69.48, 2.9) * mm});
            skLineSegment(sketch, "E317.right", {"start": v(-66.22, 14.14) * mm, "end": v(-66.22, 2.9) * mm});
            skPoint(sketch, "E317.middle", {"position": v(-67.85, 8.52) * mm});
            skLineSegment(sketch, "E318.bottom", {"start": v(-61.86, 14.14) * mm, "end": v(-59.14, 14.14) * mm});
            skLineSegment(sketch, "E318.top", {"start": v(-61.86, 2.9) * mm, "end": v(-59.14, 2.9) * mm});
            skLineSegment(sketch, "E318.left", {"start": v(-61.86, 14.14) * mm, "end": v(-61.86, 2.9) * mm});
            skLineSegment(sketch, "E318.right", {"start": v(-59.14, 14.14) * mm, "end": v(-59.14, 2.9) * mm});
            skPoint(sketch, "E318.middle", {"position": v(-60.5, 8.52) * mm});
            skEllipse(sketch, "E319", {"center": v(-52.06, 8.52) * mm, "majorRadius": 4.63 * mm, "minorRadius": 2.73 * mm, "majorAxis": v(0, 1)});
            skLineSegment(sketch, "E320.bottom", {"start": v(-43.57, 14.14) * mm, "end": v(-40.96, 14.14) * mm});
            skLineSegment(sketch, "E320.top", {"start": v(-43.57, 2.9) * mm, "end": v(-40.96, 2.9) * mm});
            skLineSegment(sketch, "E320.left", {"start": v(-43.57, 14.14) * mm, "end": v(-43.57, 2.9) * mm});
            skLineSegment(sketch, "E320.right", {"start": v(-40.96, 14.14) * mm, "end": v(-40.96, 2.9) * mm});
            skPoint(sketch, "E320.middle", {"position": v(-42.27, 8.52) * mm});
            skLineSegment(sketch, "E321.bottom", {"start": v(-37.26, 14.14) * mm, "end": v(-34.67, 14.14) * mm});
            skLineSegment(sketch, "E321.top", {"start": v(-37.26, 2.9) * mm, "end": v(-34.67, 2.9) * mm});
            skLineSegment(sketch, "E321.left", {"start": v(-37.26, 14.14) * mm, "end": v(-37.26, 2.9) * mm});
            skLineSegment(sketch, "E321.right", {"start": v(-34.67, 14.14) * mm, "end": v(-34.67, 2.9) * mm});
            skPoint(sketch, "E321.middle", {"position": v(-35.96, 8.52) * mm});
            skEllipse(sketch, "E322", {"center": v(-28.03, 8.52) * mm, "majorRadius": 3.55 * mm, "minorRadius": 3.24 * mm, "majorAxis": v(0, 1)});
            skLineSegment(sketch, "E323.bottom", {"start": v(-4.73, 14.14) * mm, "end": v(-2.55, 14.14) * mm});
            skLineSegment(sketch, "E323.top", {"start": v(-4.73, 2.9) * mm, "end": v(-2.55, 2.9) * mm});
            skLineSegment(sketch, "E323.left", {"start": v(-4.73, 14.14) * mm, "end": v(-4.73, 2.9) * mm});
            skLineSegment(sketch, "E323.right", {"start": v(-2.55, 14.14) * mm, "end": v(-2.55, 2.9) * mm});
            skPoint(sketch, "E323.middle", {"position": v(-3.64, 8.52) * mm});
            skEllipse(sketch, "E324", {"center": v(-10.17, 8.52) * mm, "majorRadius": 3.27 * mm, "minorRadius": 2.06 * mm, "majorAxis": v(0, 1)});
            skLineSegment(sketch, "E325.bottom", {"start": v(-22.96, 14.14) * mm, "end": v(-20.24, 14.14) * mm});
            skLineSegment(sketch, "E325.top", {"start": v(-22.96, 2.9) * mm, "end": v(-20.24, 2.9) * mm});
            skLineSegment(sketch, "E325.left", {"start": v(-22.96, 14.14) * mm, "end": v(-22.96, 2.9) * mm});
            skLineSegment(sketch, "E325.right", {"start": v(-20.24, 14.14) * mm, "end": v(-20.24, 2.9) * mm});
            skPoint(sketch, "E325.middle", {"position": v(-21.6, 8.52) * mm});
            skLineSegment(sketch, "E326.bottom", {"start": v(-16.98, 14.14) * mm, "end": v(-14.8, 14.14) * mm});
            skLineSegment(sketch, "E326.top", {"start": v(-16.98, 2.9) * mm, "end": v(-14.8, 2.9) * mm});
            skLineSegment(sketch, "E326.left", {"start": v(-16.98, 14.14) * mm, "end": v(-16.98, 2.9) * mm});
            skLineSegment(sketch, "E326.right", {"start": v(-14.8, 14.14) * mm, "end": v(-14.8, 2.9) * mm});
            skPoint(sketch, "E326.middle", {"position": v(-15.89, 8.52) * mm});
            skLineSegment(sketch, "E327.MirrorCS", {"start": v(83.9, 14.14) * mm, "end": v(85.54, 14.14) * mm});
            skLineSegment(sketch, "E328.MirrorCS", {"start": v(16.98, 14.14) * mm, "end": v(14.8, 14.14) * mm});
            skLineSegment(sketch, "E329.MirrorCS", {"start": v(16.98, 2.9) * mm, "end": v(14.8, 2.9) * mm});
            skLineSegment(sketch, "E330.MirrorCS", {"start": v(37.26, 2.9) * mm, "end": v(34.67, 2.9) * mm});
            skLineSegment(sketch, "E331.MirrorCS", {"start": v(43.57, 14.14) * mm, "end": v(40.96, 14.14) * mm});
            skLineSegment(sketch, "E332.MirrorCS", {"start": v(43.57, 2.9) * mm, "end": v(40.96, 2.9) * mm});
            skLineSegment(sketch, "E333.MirrorCS", {"start": v(22.96, 2.9) * mm, "end": v(20.24, 2.9) * mm});
            skLineSegment(sketch, "E334.MirrorCS", {"start": v(69.48, 14.14) * mm, "end": v(66.22, 14.14) * mm});
            skLineSegment(sketch, "E335.MirrorCS", {"start": v(37.26, 14.14) * mm, "end": v(34.67, 14.14) * mm});
            skLineSegment(sketch, "E336.MirrorCS", {"start": v(4.73, 2.9) * mm, "end": v(2.55, 2.9) * mm});
            skLineSegment(sketch, "E337.MirrorCS", {"start": v(69.48, 2.9) * mm, "end": v(66.22, 2.9) * mm});
            skLineSegment(sketch, "E338.MirrorCS", {"start": v(83.9, 2.9) * mm, "end": v(85.54, 2.9) * mm});
            skLineSegment(sketch, "E339.MirrorCS", {"start": v(61.86, 2.9) * mm, "end": v(59.14, 2.9) * mm});
            skLineSegment(sketch, "E340.MirrorCS", {"start": v(22.96, 14.14) * mm, "end": v(20.24, 14.14) * mm});
            skLineSegment(sketch, "E341.MirrorCS", {"start": v(4.73, 14.14) * mm, "end": v(2.55, 14.14) * mm});
            skLineSegment(sketch, "E342.MirrorCS", {"start": v(61.86, 14.14) * mm, "end": v(59.14, 14.14) * mm});
            skEllipse(sketch, "E343.MirrorC", {"center": v(52.06, 8.52) * mm, "majorRadius": 4.63 * mm, "minorRadius": 2.73 * mm, "majorAxis": v(0, 1)});
            skPoint(sketch, "E344.MirrorP", {"position": v(21.6, 8.52) * mm});
            skLineSegment(sketch, "E345.MirrorCS", {"start": v(14.8, 14.14) * mm, "end": v(14.8, 2.9) * mm});
            skLineSegment(sketch, "E346.MirrorCS", {"start": v(22.96, 14.14) * mm, "end": v(22.96, 2.9) * mm});
            skLineSegment(sketch, "E347.MirrorCS", {"start": v(4.73, 14.14) * mm, "end": v(4.73, 2.9) * mm});
            skLineSegment(sketch, "E348.MirrorCS", {"start": v(83.9, 14.14) * mm, "end": v(83.9, 2.9) * mm});
            skPoint(sketch, "E349.MirrorP", {"position": v(15.89, 8.52) * mm});
            skLineSegment(sketch, "E350.MirrorCS", {"start": v(85.54, 14.14) * mm, "end": v(85.54, 2.9) * mm});
            skPoint(sketch, "E351.MirrorP", {"position": v(67.85, 8.52) * mm});
            skLineSegment(sketch, "E352.MirrorCS", {"start": v(43.57, 14.14) * mm, "end": v(43.57, 2.9) * mm});
            skLineSegment(sketch, "E353.MirrorCS", {"start": v(66.22, 14.14) * mm, "end": v(66.22, 2.9) * mm});
            skLineSegment(sketch, "E354.MirrorCS", {"start": v(59.14, 14.14) * mm, "end": v(59.14, 2.9) * mm});
            skPoint(sketch, "E355.MirrorP", {"position": v(84.73, 8.52) * mm});
            skLineSegment(sketch, "E356.MirrorCS", {"start": v(2.55, 14.14) * mm, "end": v(2.55, 2.9) * mm});
            skLineSegment(sketch, "E357.MirrorCS", {"start": v(61.86, 14.14) * mm, "end": v(61.86, 2.9) * mm});
            skLineSegment(sketch, "E358.MirrorCS", {"start": v(69.48, 14.14) * mm, "end": v(69.48, 2.9) * mm});
            skEllipse(sketch, "E359.MirrorC", {"center": v(10.17, 8.52) * mm, "majorRadius": 3.27 * mm, "minorRadius": 2.06 * mm, "majorAxis": v(0, 1)});
            skPoint(sketch, "E360.MirrorP", {"position": v(35.96, 8.52) * mm});
            skPoint(sketch, "E361.MirrorP", {"position": v(60.5, 8.52) * mm});
            skLineSegment(sketch, "E362.MirrorCS", {"start": v(16.98, 14.14) * mm, "end": v(16.98, 2.9) * mm});
            skLineSegment(sketch, "E363.MirrorCS", {"start": v(40.96, 14.14) * mm, "end": v(40.96, 2.9) * mm});
            skLineSegment(sketch, "E364.MirrorCS", {"start": v(34.67, 14.14) * mm, "end": v(34.67, 2.9) * mm});
            skPoint(sketch, "E365.MirrorP", {"position": v(42.27, 8.52) * mm});
            skCircle(sketch, "E366.MirrorC", {"center": v(77.1, 8.52) * mm, "radius": 3.7 * mm});
            skLineSegment(sketch, "E367.MirrorCS", {"start": v(37.26, 14.14) * mm, "end": v(37.26, 2.9) * mm});
            skLineSegment(sketch, "E368.MirrorCS", {"start": v(20.24, 14.14) * mm, "end": v(20.24, 2.9) * mm});
            skPoint(sketch, "E369.MirrorP", {"position": v(3.64, 8.52) * mm});
            skEllipse(sketch, "E370.MirrorC", {"center": v(28.03, 8.52) * mm, "majorRadius": 3.55 * mm, "minorRadius": 3.24 * mm, "majorAxis": v(0, 1)});
            skEllipse(sketch, "E371.MirrorC", {"center": v(-28.03, 8.52) * mm, "majorRadius": 3.55 * mm, "minorRadius": 3.24 * mm, "majorAxis": v(0, 1)});
            skEllipse(sketch, "E372.MirrorC", {"center": v(-10.17, 8.52) * mm, "majorRadius": 3.27 * mm, "minorRadius": 2.06 * mm, "majorAxis": v(0, 1)});
            skEllipse(sketch, "E373.MirrorC", {"center": v(28.03, 8.52) * mm, "majorRadius": 3.55 * mm, "minorRadius": 3.24 * mm, "majorAxis": v(0, 1)});
            skEllipse(sketch, "E374.MirrorC", {"center": v(10.17, 8.52) * mm, "majorRadius": 3.27 * mm, "minorRadius": 2.06 * mm, "majorAxis": v(0, 1)});
            skEllipse(sketch, "E375.MirrorC", {"center": v(-52.06, 8.52) * mm, "majorRadius": 4.63 * mm, "minorRadius": 2.73 * mm, "majorAxis": v(0, 1)});
            skEllipse(sketch, "E376.MirrorC", {"center": v(52.06, 8.52) * mm, "majorRadius": 4.63 * mm, "minorRadius": 2.73 * mm, "majorAxis": v(0, 1)});
            skEllipse(sketch, "E377.MirrorC", {"center": v(10.17, 8.52) * mm, "majorRadius": 3.27 * mm, "minorRadius": 2.06 * mm, "majorAxis": v(0, 1)});
            skEllipse(sketch, "E378.MirrorC", {"center": v(10.17, 8.52) * mm, "majorRadius": 3.27 * mm, "minorRadius": 2.06 * mm, "majorAxis": v(0, 1)});
            skEllipse(sketch, "E379.MirrorC", {"center": v(-10.17, 8.52) * mm, "majorRadius": 3.27 * mm, "minorRadius": 2.06 * mm, "majorAxis": v(0, 1)});
            skEllipse(sketch, "E380.MirrorC", {"center": v(-10.17, 8.52) * mm, "majorRadius": 3.27 * mm, "minorRadius": 2.06 * mm, "majorAxis": v(0, 1)});
            skEllipse(sketch, "E381.MirrorC", {"center": v(-28.03, 8.52) * mm, "majorRadius": 3.55 * mm, "minorRadius": 3.24 * mm, "majorAxis": v(0, 1)});
            skEllipse(sketch, "E382.MirrorC", {"center": v(28.03, 8.52) * mm, "majorRadius": 3.55 * mm, "minorRadius": 3.24 * mm, "majorAxis": v(0, 1)});
            skEllipse(sketch, "E383.MirrorC", {"center": v(-28.03, 8.52) * mm, "majorRadius": 3.55 * mm, "minorRadius": 3.24 * mm, "majorAxis": v(0, 1)});
            skEllipse(sketch, "E384.MirrorC", {"center": v(28.03, 8.52) * mm, "majorRadius": 3.55 * mm, "minorRadius": 3.24 * mm, "majorAxis": v(0, 1)});
            skLineSegment(sketch, "E385.MirrorCS", {"start": v(6.91, 19.72) * mm, "end": v(6.91, 16.63) * mm});
            skLineSegment(sketch, "E386.MirrorCS", {"start": v(55.55, 19.72) * mm, "end": v(55.55, 16.63) * mm});
            skEllipse(sketch, "E387.MirrorC", {"center": v(52.06, 8.52) * mm, "majorRadius": 4.63 * mm, "minorRadius": 2.73 * mm, "majorAxis": v(0, 1)});
            skEllipse(sketch, "E388.MirrorC", {"center": v(-52.06, 8.52) * mm, "majorRadius": 4.63 * mm, "minorRadius": 2.73 * mm, "majorAxis": v(0, 1)});
            skEllipse(sketch, "E389.MirrorC", {"center": v(52.06, 8.52) * mm, "majorRadius": 4.63 * mm, "minorRadius": 2.73 * mm, "majorAxis": v(0, 1)});
            skEllipse(sketch, "E390.MirrorC", {"center": v(-52.06, 8.52) * mm, "majorRadius": 4.63 * mm, "minorRadius": 2.73 * mm, "majorAxis": v(0, 1)});
            skLineSegment(sketch, "E391.MirrorCS", {"start": v(88.8, 8.52) * mm, "end": v(0, 8.52) * mm, "construction": true});
            skLineSegment(sketch, "E392.MirrorCS", {"start": v(55.55, 16.63) * mm, "end": v(6.91, 16.63) * mm});
            skLineSegment(sketch, "E393.MirrorCS", {"start": v(-55.55, 19.7) * mm, "end": v(-6.91, 19.7) * mm});
            skLineSegment(sketch, "E394.MirrorCS", {"start": v(55.55, 19.72) * mm, "end": v(6.91, 19.72) * mm});
            skLineSegment(sketch, "E395.MirrorCS", {"start": v(83.9, 87.61) * mm, "end": v(85.54, 87.61) * mm});
            skLineSegment(sketch, "E396.MirrorCS", {"start": v(4.73, 87.61) * mm, "end": v(2.55, 87.61) * mm});
            skLineSegment(sketch, "E397.MirrorCS", {"start": v(-43.57, 87.61) * mm, "end": v(-40.96, 87.61) * mm});
            skLineSegment(sketch, "E398.MirrorCS", {"start": v(16.98, 87.61) * mm, "end": v(14.8, 87.61) * mm});
            skLineSegment(sketch, "E399.MirrorCS", {"start": v(43.57, 87.61) * mm, "end": v(40.96, 87.61) * mm});
            skLineSegment(sketch, "E400.MirrorCS", {"start": v(22.96, 87.61) * mm, "end": v(20.24, 87.61) * mm});
            skLineSegment(sketch, "E401.MirrorCS", {"start": v(-16.98, 87.61) * mm, "end": v(-14.8, 87.61) * mm});
            skLineSegment(sketch, "E402.MirrorCS", {"start": v(-61.86, 87.61) * mm, "end": v(-59.14, 87.61) * mm});
            skLineSegment(sketch, "E403.MirrorCS", {"start": v(-69.48, 87.61) * mm, "end": v(-66.22, 87.61) * mm});
            skLineSegment(sketch, "E404.MirrorCS", {"start": v(61.86, 87.61) * mm, "end": v(59.14, 87.61) * mm});
            skLineSegment(sketch, "E405.MirrorCS", {"start": v(69.48, 87.61) * mm, "end": v(66.22, 87.61) * mm});
            skLineSegment(sketch, "E406.MirrorCS", {"start": v(37.26, 87.61) * mm, "end": v(34.67, 87.61) * mm});
            skLineSegment(sketch, "E407.MirrorCS", {"start": v(-4.73, 87.61) * mm, "end": v(-2.55, 87.61) * mm});
            skLineSegment(sketch, "E408.MirrorCS", {"start": v(-37.26, 87.61) * mm, "end": v(-34.67, 87.61) * mm});
            skLineSegment(sketch, "E409.MirrorCS", {"start": v(-22.96, 87.61) * mm, "end": v(-20.24, 87.61) * mm});
            skLineSegment(sketch, "E410.MirrorCS", {"start": v(-83.9, 87.61) * mm, "end": v(-85.54, 87.61) * mm});
            skLineSegment(sketch, "E411.MirrorCS", {"start": v(43.57, 87.61) * mm, "end": v(43.57, 98.85) * mm});
            skLineSegment(sketch, "E412.MirrorCS", {"start": v(-4.73, 87.61) * mm, "end": v(-4.73, 98.85) * mm});
            skEllipse(sketch, "E413.MirrorC", {"center": v(10.17, 93.23) * mm, "majorRadius": 3.27 * mm, "minorRadius": 2.06 * mm, "majorAxis": v(0, -1)});
            skPoint(sketch, "E414.MirrorP", {"position": v(-60.5, 93.23) * mm});
            skEllipse(sketch, "E415.MirrorC", {"center": v(-28.03, 93.23) * mm, "majorRadius": 3.55 * mm, "minorRadius": 3.24 * mm, "majorAxis": v(0, -1)});
            skLineSegment(sketch, "E416.MirrorCS", {"start": v(-83.9, 87.61) * mm, "end": v(-83.9, 98.85) * mm});
            skPoint(sketch, "E417.MirrorP", {"position": v(67.85, 93.23) * mm});
            skLineSegment(sketch, "E418.MirrorCS", {"start": v(-37.26, 98.85) * mm, "end": v(-34.67, 98.85) * mm});
            skLineSegment(sketch, "E419.MirrorCS", {"start": v(4.73, 98.85) * mm, "end": v(2.55, 98.85) * mm});
            skLineSegment(sketch, "E420.MirrorCS", {"start": v(61.86, 87.61) * mm, "end": v(61.86, 98.85) * mm});
            skPoint(sketch, "E421.MirrorP", {"position": v(21.6, 93.23) * mm});
            skLineSegment(sketch, "E422.MirrorCS", {"start": v(-22.96, 87.61) * mm, "end": v(-22.96, 98.85) * mm});
            skLineSegment(sketch, "E423.MirrorCS", {"start": v(-14.8, 87.61) * mm, "end": v(-14.8, 98.85) * mm});
            skLineSegment(sketch, "E424.MirrorCS", {"start": v(22.96, 98.85) * mm, "end": v(20.24, 98.85) * mm});
            skLineSegment(sketch, "E425.MirrorCS", {"start": v(-66.22, 87.61) * mm, "end": v(-66.22, 98.85) * mm});
            skLineSegment(sketch, "E426.MirrorCS", {"start": v(-85.54, 87.61) * mm, "end": v(-85.54, 98.85) * mm});
            skPoint(sketch, "E427.MirrorP", {"position": v(60.5, 93.23) * mm});
            skLineSegment(sketch, "E428.MirrorCS", {"start": v(16.98, 98.85) * mm, "end": v(14.8, 98.85) * mm});
            skLineSegment(sketch, "E429.MirrorCS", {"start": v(61.86, 98.85) * mm, "end": v(59.14, 98.85) * mm});
            skLineSegment(sketch, "E430.MirrorCS", {"start": v(85.54, 87.61) * mm, "end": v(85.54, 98.85) * mm});
            skLineSegment(sketch, "E431.MirrorCS", {"start": v(-22.96, 98.85) * mm, "end": v(-20.24, 98.85) * mm});
            skEllipse(sketch, "E432.MirrorC", {"center": v(52.06, 93.23) * mm, "majorRadius": 4.63 * mm, "minorRadius": 2.73 * mm, "majorAxis": v(0, -1)});
            skPoint(sketch, "E433.MirrorP", {"position": v(-84.73, 93.23) * mm});
            skLineSegment(sketch, "E434.MirrorCS", {"start": v(69.48, 98.85) * mm, "end": v(66.22, 98.85) * mm});
            skLineSegment(sketch, "E435.MirrorCS", {"start": v(20.24, 87.61) * mm, "end": v(20.24, 98.85) * mm});
            skLineSegment(sketch, "E436.MirrorCS", {"start": v(34.67, 87.61) * mm, "end": v(34.67, 98.85) * mm});
            skPoint(sketch, "E437.MirrorP", {"position": v(-15.89, 93.23) * mm});
            skCircle(sketch, "E438.MirrorC", {"center": v(77.1, 93.23) * mm, "radius": 3.7 * mm});
            skLineSegment(sketch, "E439.MirrorCS", {"start": v(59.14, 87.61) * mm, "end": v(59.14, 98.85) * mm});
            skLineSegment(sketch, "E440.MirrorCS", {"start": v(83.9, 98.85) * mm, "end": v(85.54, 98.85) * mm});
            skPoint(sketch, "E441.MirrorP", {"position": v(42.27, 93.23) * mm});
            skPoint(sketch, "E442.MirrorP", {"position": v(-35.96, 93.23) * mm});
            skPoint(sketch, "E443.MirrorP", {"position": v(3.64, 93.23) * mm});
            skPoint(sketch, "E444.MirrorP", {"position": v(15.89, 93.23) * mm});
            skPoint(sketch, "E445.MirrorP", {"position": v(35.96, 93.23) * mm});
            skLineSegment(sketch, "E446.MirrorCS", {"start": v(22.96, 87.61) * mm, "end": v(22.96, 98.85) * mm});
            skLineSegment(sketch, "E447.MirrorCS", {"start": v(-61.86, 98.85) * mm, "end": v(-59.14, 98.85) * mm});
            skLineSegment(sketch, "E448.MirrorCS", {"start": v(37.26, 87.61) * mm, "end": v(37.26, 98.85) * mm});
            skPoint(sketch, "E449.MirrorP", {"position": v(-42.27, 93.23) * mm});
            skLineSegment(sketch, "E450.MirrorCS", {"start": v(40.96, 87.61) * mm, "end": v(40.96, 98.85) * mm});
            skLineSegment(sketch, "E451.MirrorCS", {"start": v(16.98, 87.61) * mm, "end": v(16.98, 98.85) * mm});
            skLineSegment(sketch, "E452.MirrorCS", {"start": v(-61.86, 87.61) * mm, "end": v(-61.86, 98.85) * mm});
            skLineSegment(sketch, "E453.MirrorCS", {"start": v(-20.24, 87.61) * mm, "end": v(-20.24, 98.85) * mm});
            skLineSegment(sketch, "E454.MirrorCS", {"start": v(-34.67, 87.61) * mm, "end": v(-34.67, 98.85) * mm});
            skLineSegment(sketch, "E455.MirrorCS", {"start": v(-83.9, 98.85) * mm, "end": v(-85.54, 98.85) * mm});
            skLineSegment(sketch, "E456.MirrorCS", {"start": v(-2.55, 87.61) * mm, "end": v(-2.55, 98.85) * mm});
            skLineSegment(sketch, "E457.MirrorCS", {"start": v(-16.98, 98.85) * mm, "end": v(-14.8, 98.85) * mm});
            skLineSegment(sketch, "E458.MirrorCS", {"start": v(83.9, 87.61) * mm, "end": v(83.9, 98.85) * mm});
            skLineSegment(sketch, "E459.MirrorCS", {"start": v(4.73, 87.61) * mm, "end": v(4.73, 98.85) * mm});
            skLineSegment(sketch, "E460.MirrorCS", {"start": v(-59.14, 87.61) * mm, "end": v(-59.14, 98.85) * mm});
            skPoint(sketch, "E461.MirrorP", {"position": v(-21.6, 93.23) * mm});
            skEllipse(sketch, "E462.MirrorC", {"center": v(28.03, 93.23) * mm, "majorRadius": 3.55 * mm, "minorRadius": 3.24 * mm, "majorAxis": v(0, -1)});
            skLineSegment(sketch, "E463.MirrorCS", {"start": v(-43.57, 87.61) * mm, "end": v(-43.57, 98.85) * mm});
            skLineSegment(sketch, "E464.MirrorCS", {"start": v(2.55, 87.61) * mm, "end": v(2.55, 98.85) * mm});
            skLineSegment(sketch, "E465.MirrorCS", {"start": v(43.57, 98.85) * mm, "end": v(40.96, 98.85) * mm});
            skEllipse(sketch, "E466.MirrorC", {"center": v(-52.06, 93.23) * mm, "majorRadius": 4.63 * mm, "minorRadius": 2.73 * mm, "majorAxis": v(0, -1)});
            skLineSegment(sketch, "E467.MirrorCS", {"start": v(66.22, 87.61) * mm, "end": v(66.22, 98.85) * mm});
            skLineSegment(sketch, "E468.MirrorCS", {"start": v(69.48, 87.61) * mm, "end": v(69.48, 98.85) * mm});
            skLineSegment(sketch, "E469.MirrorCS", {"start": v(-69.48, 98.85) * mm, "end": v(-66.22, 98.85) * mm});
            skEllipse(sketch, "E470.MirrorC", {"center": v(-10.17, 93.23) * mm, "majorRadius": 3.27 * mm, "minorRadius": 2.06 * mm, "majorAxis": v(0, -1)});
            skLineSegment(sketch, "E471.MirrorCS", {"start": v(-43.57, 98.85) * mm, "end": v(-40.96, 98.85) * mm});
            skLineSegment(sketch, "E472.MirrorCS", {"start": v(37.26, 98.85) * mm, "end": v(34.67, 98.85) * mm});
            skLineSegment(sketch, "E473.MirrorCS", {"start": v(-37.26, 87.61) * mm, "end": v(-37.26, 98.85) * mm});
            skLineSegment(sketch, "E474.MirrorCS", {"start": v(14.8, 87.61) * mm, "end": v(14.8, 98.85) * mm});
            skPoint(sketch, "E475.MirrorP", {"position": v(-3.64, 93.23) * mm});
            skLineSegment(sketch, "E476.MirrorCS", {"start": v(-4.73, 98.85) * mm, "end": v(-2.55, 98.85) * mm});
            skCircle(sketch, "E477.MirrorC", {"center": v(-77.1, 93.23) * mm, "radius": 3.7 * mm});
            skPoint(sketch, "E478.MirrorP", {"position": v(-67.85, 93.23) * mm});
            skLineSegment(sketch, "E479.MirrorCS", {"start": v(-16.98, 87.61) * mm, "end": v(-16.98, 98.85) * mm});
            skPoint(sketch, "E480.MirrorP", {"position": v(84.73, 93.23) * mm});
            skLineSegment(sketch, "E481.MirrorCS", {"start": v(-69.48, 87.61) * mm, "end": v(-69.48, 98.85) * mm});
            skLineSegment(sketch, "E482.MirrorCS", {"start": v(-40.96, 87.61) * mm, "end": v(-40.96, 98.85) * mm});
            skEllipse(sketch, "E483.MirrorC", {"center": v(10.17, 93.23) * mm, "majorRadius": 3.27 * mm, "minorRadius": 2.06 * mm, "majorAxis": v(0, -1)});
            skEllipse(sketch, "E484.MirrorC", {"center": v(28.03, 93.23) * mm, "majorRadius": 3.55 * mm, "minorRadius": 3.24 * mm, "majorAxis": v(0, -1)});
            skEllipse(sketch, "E485.MirrorC", {"center": v(52.06, 93.23) * mm, "majorRadius": 4.63 * mm, "minorRadius": 2.73 * mm, "majorAxis": v(0, -1)});
            skEllipse(sketch, "E486.MirrorC", {"center": v(-28.03, 93.23) * mm, "majorRadius": 3.55 * mm, "minorRadius": 3.24 * mm, "majorAxis": v(0, -1)});
            skEllipse(sketch, "E487.MirrorC", {"center": v(-10.17, 93.23) * mm, "majorRadius": 3.27 * mm, "minorRadius": 2.06 * mm, "majorAxis": v(0, -1)});
            skEllipse(sketch, "E488.MirrorC", {"center": v(-52.06, 93.23) * mm, "majorRadius": 4.63 * mm, "minorRadius": 2.73 * mm, "majorAxis": v(0, -1)});
            skEllipse(sketch, "E489.MirrorC", {"center": v(10.17, 93.23) * mm, "majorRadius": 3.27 * mm, "minorRadius": 2.06 * mm, "majorAxis": v(0, -1)});
            skEllipse(sketch, "E490.MirrorC", {"center": v(-28.03, 93.23) * mm, "majorRadius": 3.55 * mm, "minorRadius": 3.24 * mm, "majorAxis": v(0, -1)});
            skEllipse(sketch, "E491.MirrorC", {"center": v(52.06, 93.23) * mm, "majorRadius": 4.63 * mm, "minorRadius": 2.73 * mm, "majorAxis": v(0, -1)});
            skEllipse(sketch, "E492.MirrorC", {"center": v(28.03, 93.23) * mm, "majorRadius": 3.55 * mm, "minorRadius": 3.24 * mm, "majorAxis": v(0, -1)});
            skEllipse(sketch, "E493.MirrorC", {"center": v(-10.17, 93.23) * mm, "majorRadius": 3.27 * mm, "minorRadius": 2.06 * mm, "majorAxis": v(0, -1)});
            skEllipse(sketch, "E494.MirrorC", {"center": v(-52.06, 93.23) * mm, "majorRadius": 4.63 * mm, "minorRadius": 2.73 * mm, "majorAxis": v(0, -1)});
            skEllipse(sketch, "E495.MirrorC", {"center": v(-28.03, 93.23) * mm, "majorRadius": 3.55 * mm, "minorRadius": 3.24 * mm, "majorAxis": v(0, -1)});
            skEllipse(sketch, "E496.MirrorC", {"center": v(-10.17, 93.23) * mm, "majorRadius": 3.27 * mm, "minorRadius": 2.06 * mm, "majorAxis": v(0, -1)});
            skEllipse(sketch, "E497.MirrorC", {"center": v(28.03, 93.23) * mm, "majorRadius": 3.55 * mm, "minorRadius": 3.24 * mm, "majorAxis": v(0, -1)});
            skEllipse(sketch, "E498.MirrorC", {"center": v(10.17, 93.23) * mm, "majorRadius": 3.27 * mm, "minorRadius": 2.06 * mm, "majorAxis": v(0, -1)});
            skEllipse(sketch, "E499.MirrorC", {"center": v(52.06, 93.23) * mm, "majorRadius": 4.63 * mm, "minorRadius": 2.73 * mm, "majorAxis": v(0, -1)});
            skEllipse(sketch, "E500.MirrorC", {"center": v(-52.06, 93.23) * mm, "majorRadius": 4.63 * mm, "minorRadius": 2.73 * mm, "majorAxis": v(0, -1)});
            skLineSegment(sketch, "E501", {"start": v(-87.13, 83.97) * mm, "end": v(-87.13, 74.95) * mm});
            skLineSegment(sketch, "E502", {"start": v(-87.13, 74.95) * mm, "end": v(-77.27, 78.94) * mm});
            skLineSegment(sketch, "E503", {"start": v(-77.27, 78.94) * mm, "end": v(-87.13, 83.97) * mm});
            skLineSegment(sketch, "E504", {"start": v(-75.03, 76.46) * mm, "end": v(-82.1, 74.53) * mm});
            skLineSegment(sketch, "E505", {"start": v(-82.1, 74.53) * mm, "end": v(-75.03, 68.43) * mm});
            skLineSegment(sketch, "E506", {"start": v(-75.03, 68.43) * mm, "end": v(-75.03, 76.46) * mm});
            skLineSegment(sketch, "E507", {"start": v(-87.13, 68.86) * mm, "end": v(-87.13, 61.52) * mm});
            skLineSegment(sketch, "E508", {"start": v(-87.13, 61.52) * mm, "end": v(-77.27, 67.4) * mm});
            skLineSegment(sketch, "E509", {"start": v(-77.27, 67.4) * mm, "end": v(-87.13, 68.86) * mm});
            skLineSegment(sketch, "E510", {"start": v(-75.03, 64.64) * mm, "end": v(-84.7, 58.88) * mm});
            skLineSegment(sketch, "E511", {"start": v(-84.7, 58.88) * mm, "end": v(-75.03, 57.44) * mm});
            skLineSegment(sketch, "E512", {"start": v(-75.03, 57.44) * mm, "end": v(-75.03, 64.64) * mm});
            skLineSegment(sketch, "E513", {"start": v(-86.66, 50.88) * mm, "end": v(-86.66, 55.92) * mm});
            skLineSegment(sketch, "E514", {"start": v(-86.66, 55.92) * mm, "end": v(-70.88, 50.88) * mm});
            skLineSegment(sketch, "E515.MirrorCS", {"start": v(-86.66, 50.88) * mm, "end": v(-86.66, 45.83) * mm});
            skLineSegment(sketch, "E516.MirrorCS", {"start": v(-86.66, 45.83) * mm, "end": v(-70.88, 50.88) * mm});
            skLineSegment(sketch, "E517.MirrorCS", {"start": v(-75.03, 44.3) * mm, "end": v(-75.03, 37.1) * mm});
            skLineSegment(sketch, "E518.MirrorCS", {"start": v(-77.27, 34.36) * mm, "end": v(-87.13, 32.89) * mm});
            skLineSegment(sketch, "E519.MirrorCS", {"start": v(-77.27, 22.81) * mm, "end": v(-87.13, 17.78) * mm});
            skLineSegment(sketch, "E520.MirrorCS", {"start": v(-75.03, 25.3) * mm, "end": v(-82.1, 27.22) * mm});
            skLineSegment(sketch, "E521.MirrorCS", {"start": v(-87.13, 26.8) * mm, "end": v(-77.27, 22.81) * mm});
            skLineSegment(sketch, "E522.MirrorCS", {"start": v(-84.7, 42.87) * mm, "end": v(-75.03, 44.3) * mm});
            skLineSegment(sketch, "E523.MirrorCS", {"start": v(-87.13, 40.23) * mm, "end": v(-77.27, 34.36) * mm});
            skLineSegment(sketch, "E524.MirrorCS", {"start": v(-75.03, 33.33) * mm, "end": v(-75.03, 25.3) * mm});
            skLineSegment(sketch, "E525.MirrorCS", {"start": v(-82.1, 27.22) * mm, "end": v(-75.03, 33.33) * mm});
            skLineSegment(sketch, "E526.MirrorCS", {"start": v(-87.13, 32.89) * mm, "end": v(-87.13, 40.23) * mm});
            skLineSegment(sketch, "E527.MirrorCS", {"start": v(-75.03, 37.1) * mm, "end": v(-84.7, 42.87) * mm});
            skLineSegment(sketch, "E528.MirrorCS", {"start": v(-87.13, 17.78) * mm, "end": v(-87.13, 26.8) * mm});
            skLineSegment(sketch, "E529.MirrorCS", {"start": v(86.66, 45.83) * mm, "end": v(70.88, 50.88) * mm});
            skLineSegment(sketch, "E530.MirrorCS", {"start": v(86.66, 55.92) * mm, "end": v(70.88, 50.88) * mm});
            skLineSegment(sketch, "E531.MirrorCS", {"start": v(86.66, 50.88) * mm, "end": v(86.66, 45.83) * mm});
            skLineSegment(sketch, "E532.MirrorCS", {"start": v(86.66, 50.88) * mm, "end": v(86.66, 55.92) * mm});
            skLineSegment(sketch, "E533.MirrorCS", {"start": v(75.03, 37.1) * mm, "end": v(84.7, 42.87) * mm});
            skLineSegment(sketch, "E534.MirrorCS", {"start": v(75.03, 25.3) * mm, "end": v(82.1, 27.22) * mm});
            skLineSegment(sketch, "E535.MirrorCS", {"start": v(87.13, 61.52) * mm, "end": v(77.27, 67.4) * mm});
            skLineSegment(sketch, "E536.MirrorCS", {"start": v(75.03, 33.33) * mm, "end": v(75.03, 25.3) * mm});
            skLineSegment(sketch, "E537.MirrorCS", {"start": v(82.1, 74.53) * mm, "end": v(75.03, 68.43) * mm});
            skLineSegment(sketch, "E538.MirrorCS", {"start": v(87.13, 26.8) * mm, "end": v(77.27, 22.81) * mm});
            skLineSegment(sketch, "E539.MirrorCS", {"start": v(75.03, 57.44) * mm, "end": v(75.03, 64.64) * mm});
            skLineSegment(sketch, "E540.MirrorCS", {"start": v(75.03, 68.43) * mm, "end": v(75.03, 76.46) * mm});
            skLineSegment(sketch, "E541.MirrorCS", {"start": v(77.27, 22.81) * mm, "end": v(87.13, 17.78) * mm});
            skLineSegment(sketch, "E542.MirrorCS", {"start": v(75.03, 44.3) * mm, "end": v(75.03, 37.1) * mm});
            skLineSegment(sketch, "E543.MirrorCS", {"start": v(87.13, 32.89) * mm, "end": v(87.13, 40.23) * mm});
            skLineSegment(sketch, "E544.MirrorCS", {"start": v(77.27, 78.94) * mm, "end": v(87.13, 83.97) * mm});
            skLineSegment(sketch, "E545.MirrorCS", {"start": v(87.13, 40.23) * mm, "end": v(77.27, 34.36) * mm});
            skLineSegment(sketch, "E546.MirrorCS", {"start": v(84.7, 58.88) * mm, "end": v(75.03, 57.44) * mm});
            skLineSegment(sketch, "E547.MirrorCS", {"start": v(77.27, 34.36) * mm, "end": v(87.13, 32.89) * mm});
            skLineSegment(sketch, "E548.MirrorCS", {"start": v(84.7, 42.87) * mm, "end": v(75.03, 44.3) * mm});
            skLineSegment(sketch, "E549.MirrorCS", {"start": v(82.1, 27.22) * mm, "end": v(75.03, 33.33) * mm});
            skLineSegment(sketch, "E550.MirrorCS", {"start": v(75.03, 76.46) * mm, "end": v(82.1, 74.53) * mm});
            skLineSegment(sketch, "E551.MirrorCS", {"start": v(75.03, 64.64) * mm, "end": v(84.7, 58.88) * mm});
            skLineSegment(sketch, "E552.MirrorCS", {"start": v(77.27, 67.4) * mm, "end": v(87.13, 68.86) * mm});
            skLineSegment(sketch, "E553.MirrorCS", {"start": v(87.13, 17.78) * mm, "end": v(87.13, 26.8) * mm});
            skLineSegment(sketch, "E554.MirrorCS", {"start": v(87.13, 83.97) * mm, "end": v(87.13, 74.95) * mm});
            skLineSegment(sketch, "E555.MirrorCS", {"start": v(87.13, 68.86) * mm, "end": v(87.13, 61.52) * mm});
            skLineSegment(sketch, "E556.MirrorCS", {"start": v(87.13, 74.95) * mm, "end": v(77.27, 78.94) * mm});
            skSolve(sketch);
        }
        {
            var Q0;
            Q0=qSketchRegion(id+"F8",true);
            extrude(context, id + "F9", {"entities" : qUnion([Q0]), "operationType" : NewBodyOperationType.REMOVE, "oppositeDirection" : true, "depth" : 127 * mm, "offsetDistance" : 25.4 * mm});
        }
        {
            var Q0;
            Q0=makeQuery(id+"F4.opExtrude","SWEPT_FACE",FACE,{"disambiguationData":[OSD([sQuery(id+"F3.wireOp",EDGE,"E5.bottom")])]});
            var sketch = newSketch(context, id + "F10", { "sketchPlane" : qUnion([Q0])});
            skLineSegment(sketch, "E557", {"start": v(0, 101.6) * mm, "end": v(0, 111.13) * mm, "construction": true});
            skCircle(sketch, "E558", {"center": v(0, 106.36) * mm, "radius": 1.59 * mm});
            skLineSegment(sketch, "E559", {"start": v(0, 106.36) * mm, "end": v(-88.9, 106.36) * mm, "construction": true});
            skCircle(sketch, "E560", {"center": v(-16.51, 106.36) * mm, "radius": 1.59 * mm});
            skCircle(sketch, "E561", {"center": v(-33.02, 106.36) * mm, "radius": 1.59 * mm});
            skCircle(sketch, "E562", {"center": v(-49.53, 106.36) * mm, "radius": 1.59 * mm});
            skCircle(sketch, "E563", {"center": v(-66.04, 106.36) * mm, "radius": 1.59 * mm});
            skCircle(sketch, "E564", {"center": v(-82.55, 106.36) * mm, "radius": 1.59 * mm});
            skCircle(sketch, "E565.MirrorC", {"center": v(16.5, 106.36) * mm, "radius": 1.59 * mm});
            skCircle(sketch, "E566.MirrorC", {"center": v(33.02, 106.36) * mm, "radius": 1.59 * mm});
            skCircle(sketch, "E567.MirrorC", {"center": v(49.53, 106.36) * mm, "radius": 1.59 * mm});
            skCircle(sketch, "E568.MirrorC", {"center": v(66.04, 106.36) * mm, "radius": 1.59 * mm});
            skCircle(sketch, "E569.MirrorC", {"center": v(82.55, 106.36) * mm, "radius": 1.59 * mm});
            skLineSegment(sketch, "E570", {"start": v(0, 101.6) * mm, "end": v(0, 0) * mm, "construction": true});
            skPoint(sketch, "E571", {"position": v(0, 50.8) * mm});
            skLineSegment(sketch, "E572", {"start": v(0, 50.8) * mm, "end": v(-88.78, 50.8) * mm});
            skCircle(sketch, "E573.MirrorC", {"center": v(82.55, -4.76) * mm, "radius": 1.59 * mm});
            skCircle(sketch, "E574.MirrorC", {"center": v(66.04, -4.76) * mm, "radius": 1.59 * mm});
            skCircle(sketch, "E575.MirrorC", {"center": v(49.53, -4.76) * mm, "radius": 1.59 * mm});
            skCircle(sketch, "E576.MirrorC", {"center": v(33.02, -4.76) * mm, "radius": 1.59 * mm});
            skCircle(sketch, "E577.MirrorC", {"center": v(16.5, -4.76) * mm, "radius": 1.59 * mm});
            skCircle(sketch, "E578.MirrorC", {"center": v(0, -4.76) * mm, "radius": 1.59 * mm});
            skCircle(sketch, "E579.MirrorC", {"center": v(-16.51, -4.76) * mm, "radius": 1.59 * mm});
            skCircle(sketch, "E580.MirrorC", {"center": v(-33.02, -4.76) * mm, "radius": 1.59 * mm});
            skCircle(sketch, "E581.MirrorC", {"center": v(-49.53, -4.76) * mm, "radius": 1.59 * mm});
            skCircle(sketch, "E582.MirrorC", {"center": v(-66.04, -4.76) * mm, "radius": 1.59 * mm});
            skCircle(sketch, "E583.MirrorC", {"center": v(-82.55, -4.76) * mm, "radius": 1.59 * mm});
            skSolve(sketch);
        }
        {
            var Q0;
            Q0=qSketchRegion(id+"F10",true);
            extrude(context, id + "F11", {"entities" : qUnion([Q0]), "operationType" : NewBodyOperationType.REMOVE, "oppositeDirection" : true, "depth" : 127 * mm, "offsetDistance" : 25.4 * mm});
        }
        {
            var Q0;
            Q0=makeQuery(id+"F1.opExtrude","SWEPT_FACE",FACE,{"disambiguationData":[OSD([sQuery(id+"F0.wireOp",EDGE,"E0.left")])]});
            var sketch = newSketch(context, id + "F12", { "sketchPlane" : qUnion([Q0])});
            skLineSegment(sketch, "E584", {"start": v(0, 101.6) * mm, "end": v(0, 0) * mm, "construction": true});
            skLineSegment(sketch, "E585", {"start": v(-38.1, 50.8) * mm, "end": v(38.1, 50.8) * mm, "construction": true});
            skLineSegment(sketch, "E586", {"start": v(-37.06, 92.03) * mm, "end": v(-30.53, 98.35) * mm});
            skLineSegment(sketch, "E587", {"start": v(-30.53, 98.35) * mm, "end": v(-30.53, 94.56) * mm});
            skLineSegment(sketch, "E588", {"start": v(-30.53, 94.56) * mm, "end": v(-24.56, 96.03) * mm});
            skLineSegment(sketch, "E589", {"start": v(-24.56, 96.03) * mm, "end": v(-29.12, 91.54) * mm});
            skLineSegment(sketch, "E590", {"start": v(-29.12, 91.54) * mm, "end": v(-27.35, 89.73) * mm});
            skLineSegment(sketch, "E591", {"start": v(-27.35, 89.73) * mm, "end": v(-22.31, 93.93) * mm});
            skLineSegment(sketch, "E592", {"start": v(-22.31, 93.93) * mm, "end": v(-24.45, 88.22) * mm});
            skLineSegment(sketch, "E593", {"start": v(-24.45, 88.22) * mm, "end": v(-20.23, 88.22) * mm});
            skLineSegment(sketch, "E594", {"start": v(-20.23, 88.22) * mm, "end": v(-26.8, 81.36) * mm});
            skLineSegment(sketch, "E595", {"start": v(-26.8, 81.36) * mm, "end": v(-27.44, 85.36) * mm});
            skLineSegment(sketch, "E596", {"start": v(-27.44, 85.36) * mm, "end": v(-33.12, 83.75) * mm});
            skLineSegment(sketch, "E597", {"start": v(-33.12, 83.75) * mm, "end": v(-28.21, 89.08) * mm});
            skLineSegment(sketch, "E598", {"start": v(-28.21, 89.08) * mm, "end": v(-29.85, 90.59) * mm});
            skLineSegment(sketch, "E599", {"start": v(-29.85, 90.59) * mm, "end": v(-34.82, 85.19) * mm});
            skLineSegment(sketch, "E600", {"start": v(-34.82, 85.19) * mm, "end": v(-33.2, 91.9) * mm});
            skLineSegment(sketch, "E601", {"start": v(-33.2, 91.9) * mm, "end": v(-37.06, 92.03) * mm});
            skPoint(sketch, "E602", {"position": v(0, 76.57) * mm});
            skPoint(sketch, "E603", {"position": v(0, 50.8) * mm});
            skPoint(sketch, "E604", {"position": v(-19.05, 76.57) * mm});
            skLineSegment(sketch, "E605", {"start": v(-19.05, 76.57) * mm, "end": v(-19.05, 50.8) * mm, "construction": true});
            skLineSegment(sketch, "E606.0.1.0", {"start": v(-33.12, 64.19) * mm, "end": v(-28.21, 69.52) * mm});
            skLineSegment(sketch, "E606.0.1.1", {"start": v(-24.56, 76.47) * mm, "end": v(-29.12, 71.98) * mm});
            skLineSegment(sketch, "E606.0.1.2", {"start": v(-22.31, 74.37) * mm, "end": v(-24.45, 68.66) * mm});
            skLineSegment(sketch, "E606.0.1.3", {"start": v(-20.23, 68.66) * mm, "end": v(-26.8, 61.8) * mm});
            skLineSegment(sketch, "E606.0.1.4", {"start": v(-27.35, 70.18) * mm, "end": v(-22.31, 74.37) * mm});
            skLineSegment(sketch, "E606.0.1.5", {"start": v(-29.85, 71.03) * mm, "end": v(-34.82, 65.63) * mm});
            skLineSegment(sketch, "E606.0.1.6", {"start": v(-37.06, 72.47) * mm, "end": v(-30.53, 78.8) * mm});
            skLineSegment(sketch, "E606.0.1.7", {"start": v(-27.44, 65.8) * mm, "end": v(-33.12, 64.19) * mm});
            skLineSegment(sketch, "E606.0.1.8", {"start": v(-34.82, 65.63) * mm, "end": v(-33.2, 72.33) * mm});
            skLineSegment(sketch, "E606.0.1.9", {"start": v(-30.53, 75) * mm, "end": v(-24.56, 76.47) * mm});
            skLineSegment(sketch, "E606.0.1.10", {"start": v(-24.45, 68.66) * mm, "end": v(-20.23, 68.66) * mm});
            skLineSegment(sketch, "E606.0.1.11", {"start": v(-33.2, 72.33) * mm, "end": v(-37.06, 72.47) * mm});
            skLineSegment(sketch, "E606.0.1.12", {"start": v(-26.8, 61.8) * mm, "end": v(-27.44, 65.8) * mm});
            skLineSegment(sketch, "E606.0.1.13", {"start": v(-29.12, 71.98) * mm, "end": v(-27.35, 70.18) * mm});
            skLineSegment(sketch, "E606.0.1.14", {"start": v(-30.53, 78.8) * mm, "end": v(-30.53, 75) * mm});
            skLineSegment(sketch, "E606.0.1.15", {"start": v(-28.21, 69.52) * mm, "end": v(-29.85, 71.03) * mm});
            skLineSegment(sketch, "E606.0.2.0", {"start": v(-33.12, 44.63) * mm, "end": v(-28.21, 49.97) * mm});
            skLineSegment(sketch, "E606.0.2.1", {"start": v(-24.56, 56.92) * mm, "end": v(-29.12, 52.42) * mm});
            skLineSegment(sketch, "E606.0.2.2", {"start": v(-22.31, 54.81) * mm, "end": v(-24.45, 49.1) * mm});
            skLineSegment(sketch, "E606.0.2.3", {"start": v(-20.23, 49.1) * mm, "end": v(-26.8, 42.24) * mm});
            skLineSegment(sketch, "E606.0.2.4", {"start": v(-27.35, 50.62) * mm, "end": v(-22.31, 54.81) * mm});
            skLineSegment(sketch, "E606.0.2.5", {"start": v(-29.85, 51.47) * mm, "end": v(-34.82, 46.07) * mm});
            skLineSegment(sketch, "E606.0.2.6", {"start": v(-37.06, 52.91) * mm, "end": v(-30.53, 59.23) * mm});
            skLineSegment(sketch, "E606.0.2.7", {"start": v(-27.44, 46.25) * mm, "end": v(-33.12, 44.63) * mm});
            skLineSegment(sketch, "E606.0.2.8", {"start": v(-34.82, 46.07) * mm, "end": v(-33.2, 52.77) * mm});
            skLineSegment(sketch, "E606.0.2.9", {"start": v(-30.53, 55.44) * mm, "end": v(-24.56, 56.92) * mm});
            skLineSegment(sketch, "E606.0.2.10", {"start": v(-24.45, 49.1) * mm, "end": v(-20.23, 49.1) * mm});
            skLineSegment(sketch, "E606.0.2.11", {"start": v(-33.2, 52.77) * mm, "end": v(-37.06, 52.91) * mm});
            skLineSegment(sketch, "E606.0.2.12", {"start": v(-26.8, 42.24) * mm, "end": v(-27.44, 46.25) * mm});
            skLineSegment(sketch, "E606.0.2.13", {"start": v(-29.12, 52.42) * mm, "end": v(-27.35, 50.62) * mm});
            skLineSegment(sketch, "E606.0.2.14", {"start": v(-30.53, 59.23) * mm, "end": v(-30.53, 55.44) * mm});
            skLineSegment(sketch, "E606.0.2.15", {"start": v(-28.21, 49.97) * mm, "end": v(-29.85, 51.47) * mm});
            skLineSegment(sketch, "E606.0.3.0", {"start": v(-33.12, 25.07) * mm, "end": v(-28.21, 30.4) * mm});
            skLineSegment(sketch, "E606.0.3.1", {"start": v(-24.56, 37.36) * mm, "end": v(-29.12, 32.87) * mm});
            skLineSegment(sketch, "E606.0.3.2", {"start": v(-22.31, 35.25) * mm, "end": v(-24.45, 29.54) * mm});
            skLineSegment(sketch, "E606.0.3.3", {"start": v(-20.23, 29.54) * mm, "end": v(-26.8, 22.69) * mm});
            skLineSegment(sketch, "E606.0.3.4", {"start": v(-27.35, 31.06) * mm, "end": v(-22.31, 35.25) * mm});
            skLineSegment(sketch, "E606.0.3.5", {"start": v(-29.85, 31.92) * mm, "end": v(-34.82, 26.52) * mm});
            skLineSegment(sketch, "E606.0.3.6", {"start": v(-37.06, 33.36) * mm, "end": v(-30.53, 39.67) * mm});
            skLineSegment(sketch, "E606.0.3.7", {"start": v(-27.44, 26.69) * mm, "end": v(-33.12, 25.07) * mm});
            skLineSegment(sketch, "E606.0.3.8", {"start": v(-34.82, 26.52) * mm, "end": v(-33.2, 33.22) * mm});
            skLineSegment(sketch, "E606.0.3.9", {"start": v(-30.53, 35.88) * mm, "end": v(-24.56, 37.36) * mm});
            skLineSegment(sketch, "E606.0.3.10", {"start": v(-24.45, 29.54) * mm, "end": v(-20.23, 29.54) * mm});
            skLineSegment(sketch, "E606.0.3.11", {"start": v(-33.2, 33.22) * mm, "end": v(-37.06, 33.36) * mm});
            skLineSegment(sketch, "E606.0.3.12", {"start": v(-26.8, 22.69) * mm, "end": v(-27.44, 26.69) * mm});
            skLineSegment(sketch, "E606.0.3.13", {"start": v(-29.12, 32.87) * mm, "end": v(-27.35, 31.06) * mm});
            skLineSegment(sketch, "E606.0.3.14", {"start": v(-30.53, 39.67) * mm, "end": v(-30.53, 35.88) * mm});
            skLineSegment(sketch, "E606.0.3.15", {"start": v(-28.21, 30.4) * mm, "end": v(-29.85, 31.92) * mm});
            skLineSegment(sketch, "E606.1.0.0", {"start": v(-14.07, 83.75) * mm, "end": v(-9.16, 89.08) * mm});
            skLineSegment(sketch, "E606.1.0.1", {"start": v(-5.5, 96.03) * mm, "end": v(-10.07, 91.54) * mm});
            skLineSegment(sketch, "E606.1.0.2", {"start": v(-3.26, 93.93) * mm, "end": v(-5.4, 88.22) * mm});
            skLineSegment(sketch, "E606.1.0.3", {"start": v(-1.18, 88.22) * mm, "end": v(-7.76, 81.36) * mm});
            skLineSegment(sketch, "E606.1.0.4", {"start": v(-8.3, 89.73) * mm, "end": v(-3.26, 93.93) * mm});
            skLineSegment(sketch, "E606.1.0.5", {"start": v(-10.8, 90.59) * mm, "end": v(-15.77, 85.19) * mm});
            skLineSegment(sketch, "E606.1.0.6", {"start": v(-18, 92.03) * mm, "end": v(-11.48, 98.35) * mm});
            skLineSegment(sketch, "E606.1.0.7", {"start": v(-8.39, 85.36) * mm, "end": v(-14.07, 83.75) * mm});
            skLineSegment(sketch, "E606.1.0.8", {"start": v(-15.77, 85.19) * mm, "end": v(-14.14, 91.9) * mm});
            skLineSegment(sketch, "E606.1.0.9", {"start": v(-11.48, 94.56) * mm, "end": v(-5.5, 96.03) * mm});
            skLineSegment(sketch, "E606.1.0.10", {"start": v(-5.4, 88.22) * mm, "end": v(-1.18, 88.22) * mm});
            skLineSegment(sketch, "E606.1.0.11", {"start": v(-14.14, 91.9) * mm, "end": v(-18, 92.03) * mm});
            skLineSegment(sketch, "E606.1.0.12", {"start": v(-7.76, 81.36) * mm, "end": v(-8.39, 85.36) * mm});
            skLineSegment(sketch, "E606.1.0.13", {"start": v(-10.07, 91.54) * mm, "end": v(-8.3, 89.73) * mm});
            skLineSegment(sketch, "E606.1.0.14", {"start": v(-11.48, 98.35) * mm, "end": v(-11.48, 94.56) * mm});
            skLineSegment(sketch, "E606.1.0.15", {"start": v(-9.16, 89.08) * mm, "end": v(-10.8, 90.59) * mm});
            skLineSegment(sketch, "E606.1.1.0", {"start": v(-14.07, 64.19) * mm, "end": v(-9.16, 69.52) * mm});
            skLineSegment(sketch, "E606.1.1.1", {"start": v(-5.5, 76.47) * mm, "end": v(-10.07, 71.98) * mm});
            skLineSegment(sketch, "E606.1.1.2", {"start": v(-3.26, 74.37) * mm, "end": v(-5.4, 68.66) * mm});
            skLineSegment(sketch, "E606.1.1.3", {"start": v(-1.18, 68.66) * mm, "end": v(-7.76, 61.8) * mm});
            skLineSegment(sketch, "E606.1.1.4", {"start": v(-8.3, 70.18) * mm, "end": v(-3.26, 74.37) * mm});
            skLineSegment(sketch, "E606.1.1.5", {"start": v(-10.8, 71.03) * mm, "end": v(-15.77, 65.63) * mm});
            skLineSegment(sketch, "E606.1.1.6", {"start": v(-18, 72.47) * mm, "end": v(-11.48, 78.8) * mm});
            skLineSegment(sketch, "E606.1.1.7", {"start": v(-8.39, 65.8) * mm, "end": v(-14.07, 64.19) * mm});
            skLineSegment(sketch, "E606.1.1.8", {"start": v(-15.77, 65.63) * mm, "end": v(-14.14, 72.33) * mm});
            skLineSegment(sketch, "E606.1.1.9", {"start": v(-11.48, 75) * mm, "end": v(-5.5, 76.47) * mm});
            skLineSegment(sketch, "E606.1.1.10", {"start": v(-5.4, 68.66) * mm, "end": v(-1.18, 68.66) * mm});
            skLineSegment(sketch, "E606.1.1.11", {"start": v(-14.14, 72.33) * mm, "end": v(-18, 72.47) * mm});
            skLineSegment(sketch, "E606.1.1.12", {"start": v(-7.76, 61.8) * mm, "end": v(-8.39, 65.8) * mm});
            skLineSegment(sketch, "E606.1.1.13", {"start": v(-10.07, 71.98) * mm, "end": v(-8.3, 70.18) * mm});
            skLineSegment(sketch, "E606.1.1.14", {"start": v(-11.48, 78.8) * mm, "end": v(-11.48, 75) * mm});
            skLineSegment(sketch, "E606.1.1.15", {"start": v(-9.16, 69.52) * mm, "end": v(-10.8, 71.03) * mm});
            skLineSegment(sketch, "E606.1.2.0", {"start": v(-14.07, 44.63) * mm, "end": v(-9.16, 49.97) * mm});
            skLineSegment(sketch, "E606.1.2.1", {"start": v(-5.5, 56.92) * mm, "end": v(-10.07, 52.42) * mm});
            skLineSegment(sketch, "E606.1.2.2", {"start": v(-3.26, 54.81) * mm, "end": v(-5.4, 49.1) * mm});
            skLineSegment(sketch, "E606.1.2.3", {"start": v(-1.18, 49.1) * mm, "end": v(-7.76, 42.24) * mm});
            skLineSegment(sketch, "E606.1.2.4", {"start": v(-8.3, 50.62) * mm, "end": v(-3.26, 54.81) * mm});
            skLineSegment(sketch, "E606.1.2.5", {"start": v(-10.8, 51.47) * mm, "end": v(-15.77, 46.07) * mm});
            skLineSegment(sketch, "E606.1.2.6", {"start": v(-18, 52.91) * mm, "end": v(-11.48, 59.23) * mm});
            skLineSegment(sketch, "E606.1.2.7", {"start": v(-8.39, 46.25) * mm, "end": v(-14.07, 44.63) * mm});
            skLineSegment(sketch, "E606.1.2.8", {"start": v(-15.77, 46.07) * mm, "end": v(-14.14, 52.77) * mm});
            skLineSegment(sketch, "E606.1.2.9", {"start": v(-11.48, 55.44) * mm, "end": v(-5.5, 56.92) * mm});
            skLineSegment(sketch, "E606.1.2.10", {"start": v(-5.4, 49.1) * mm, "end": v(-1.18, 49.1) * mm});
            skLineSegment(sketch, "E606.1.2.11", {"start": v(-14.14, 52.77) * mm, "end": v(-18, 52.91) * mm});
            skLineSegment(sketch, "E606.1.2.12", {"start": v(-7.76, 42.24) * mm, "end": v(-8.39, 46.25) * mm});
            skLineSegment(sketch, "E606.1.2.13", {"start": v(-10.07, 52.42) * mm, "end": v(-8.3, 50.62) * mm});
            skLineSegment(sketch, "E606.1.2.14", {"start": v(-11.48, 59.23) * mm, "end": v(-11.48, 55.44) * mm});
            skLineSegment(sketch, "E606.1.2.15", {"start": v(-9.16, 49.97) * mm, "end": v(-10.8, 51.47) * mm});
            skLineSegment(sketch, "E606.1.3.0", {"start": v(-14.07, 25.07) * mm, "end": v(-9.16, 30.4) * mm});
            skLineSegment(sketch, "E606.1.3.1", {"start": v(-5.5, 37.36) * mm, "end": v(-10.07, 32.87) * mm});
            skLineSegment(sketch, "E606.1.3.2", {"start": v(-3.26, 35.25) * mm, "end": v(-5.4, 29.54) * mm});
            skLineSegment(sketch, "E606.1.3.3", {"start": v(-1.18, 29.54) * mm, "end": v(-7.76, 22.69) * mm});
            skLineSegment(sketch, "E606.1.3.4", {"start": v(-8.3, 31.06) * mm, "end": v(-3.26, 35.25) * mm});
            skLineSegment(sketch, "E606.1.3.5", {"start": v(-10.8, 31.92) * mm, "end": v(-15.77, 26.52) * mm});
            skLineSegment(sketch, "E606.1.3.6", {"start": v(-18, 33.36) * mm, "end": v(-11.48, 39.67) * mm});
            skLineSegment(sketch, "E606.1.3.7", {"start": v(-8.39, 26.69) * mm, "end": v(-14.07, 25.07) * mm});
            skLineSegment(sketch, "E606.1.3.8", {"start": v(-15.77, 26.52) * mm, "end": v(-14.14, 33.22) * mm});
            skLineSegment(sketch, "E606.1.3.9", {"start": v(-11.48, 35.88) * mm, "end": v(-5.5, 37.36) * mm});
            skLineSegment(sketch, "E606.1.3.10", {"start": v(-5.4, 29.54) * mm, "end": v(-1.18, 29.54) * mm});
            skLineSegment(sketch, "E606.1.3.11", {"start": v(-14.14, 33.22) * mm, "end": v(-18, 33.36) * mm});
            skLineSegment(sketch, "E606.1.3.12", {"start": v(-7.76, 22.69) * mm, "end": v(-8.39, 26.69) * mm});
            skLineSegment(sketch, "E606.1.3.13", {"start": v(-10.07, 32.87) * mm, "end": v(-8.3, 31.06) * mm});
            skLineSegment(sketch, "E606.1.3.14", {"start": v(-11.48, 39.67) * mm, "end": v(-11.48, 35.88) * mm});
            skLineSegment(sketch, "E606.1.3.15", {"start": v(-9.16, 30.4) * mm, "end": v(-10.8, 31.92) * mm});
            skLineSegment(sketch, "E606.2.0.0", {"start": v(4.98, 83.75) * mm, "end": v(9.89, 89.08) * mm});
            skLineSegment(sketch, "E606.2.0.1", {"start": v(13.54, 96.03) * mm, "end": v(8.98, 91.54) * mm});
            skLineSegment(sketch, "E606.2.0.2", {"start": v(15.79, 93.93) * mm, "end": v(13.65, 88.22) * mm});
            skLineSegment(sketch, "E606.2.0.3", {"start": v(17.87, 88.22) * mm, "end": v(11.3, 81.36) * mm});
            skLineSegment(sketch, "E606.2.0.4", {"start": v(10.75, 89.73) * mm, "end": v(15.79, 93.93) * mm});
            skLineSegment(sketch, "E606.2.0.5", {"start": v(8.25, 90.59) * mm, "end": v(3.28, 85.19) * mm});
            skLineSegment(sketch, "E606.2.0.6", {"start": v(1.04, 92.03) * mm, "end": v(7.57, 98.35) * mm});
            skLineSegment(sketch, "E606.2.0.7", {"start": v(10.66, 85.36) * mm, "end": v(4.98, 83.75) * mm});
            skLineSegment(sketch, "E606.2.0.8", {"start": v(3.28, 85.19) * mm, "end": v(4.9, 91.9) * mm});
            skLineSegment(sketch, "E606.2.0.9", {"start": v(7.57, 94.56) * mm, "end": v(13.54, 96.03) * mm});
            skLineSegment(sketch, "E606.2.0.10", {"start": v(13.65, 88.22) * mm, "end": v(17.87, 88.22) * mm});
            skLineSegment(sketch, "E606.2.0.11", {"start": v(4.9, 91.9) * mm, "end": v(1.04, 92.03) * mm});
            skLineSegment(sketch, "E606.2.0.12", {"start": v(11.3, 81.36) * mm, "end": v(10.66, 85.36) * mm});
            skLineSegment(sketch, "E606.2.0.13", {"start": v(8.98, 91.54) * mm, "end": v(10.75, 89.73) * mm});
            skLineSegment(sketch, "E606.2.0.14", {"start": v(7.57, 98.35) * mm, "end": v(7.57, 94.56) * mm});
            skLineSegment(sketch, "E606.2.0.15", {"start": v(9.89, 89.08) * mm, "end": v(8.25, 90.59) * mm});
            skLineSegment(sketch, "E606.2.1.0", {"start": v(4.98, 64.19) * mm, "end": v(9.89, 69.52) * mm});
            skLineSegment(sketch, "E606.2.1.1", {"start": v(13.54, 76.47) * mm, "end": v(8.98, 71.98) * mm});
            skLineSegment(sketch, "E606.2.1.2", {"start": v(15.79, 74.37) * mm, "end": v(13.65, 68.66) * mm});
            skLineSegment(sketch, "E606.2.1.3", {"start": v(17.87, 68.66) * mm, "end": v(11.3, 61.8) * mm});
            skLineSegment(sketch, "E606.2.1.4", {"start": v(10.75, 70.18) * mm, "end": v(15.79, 74.37) * mm});
            skLineSegment(sketch, "E606.2.1.5", {"start": v(8.25, 71.03) * mm, "end": v(3.28, 65.63) * mm});
            skLineSegment(sketch, "E606.2.1.6", {"start": v(1.04, 72.47) * mm, "end": v(7.57, 78.8) * mm});
            skLineSegment(sketch, "E606.2.1.7", {"start": v(10.66, 65.8) * mm, "end": v(4.98, 64.19) * mm});
            skLineSegment(sketch, "E606.2.1.8", {"start": v(3.28, 65.63) * mm, "end": v(4.9, 72.33) * mm});
            skLineSegment(sketch, "E606.2.1.9", {"start": v(7.57, 75) * mm, "end": v(13.54, 76.47) * mm});
            skLineSegment(sketch, "E606.2.1.10", {"start": v(13.65, 68.66) * mm, "end": v(17.87, 68.66) * mm});
            skLineSegment(sketch, "E606.2.1.11", {"start": v(4.9, 72.33) * mm, "end": v(1.04, 72.47) * mm});
            skLineSegment(sketch, "E606.2.1.12", {"start": v(11.3, 61.8) * mm, "end": v(10.66, 65.8) * mm});
            skLineSegment(sketch, "E606.2.1.13", {"start": v(8.98, 71.98) * mm, "end": v(10.75, 70.18) * mm});
            skLineSegment(sketch, "E606.2.1.14", {"start": v(7.57, 78.8) * mm, "end": v(7.57, 75) * mm});
            skLineSegment(sketch, "E606.2.1.15", {"start": v(9.89, 69.52) * mm, "end": v(8.25, 71.03) * mm});
            skLineSegment(sketch, "E606.2.2.0", {"start": v(4.98, 44.63) * mm, "end": v(9.89, 49.97) * mm});
            skLineSegment(sketch, "E606.2.2.1", {"start": v(13.54, 56.92) * mm, "end": v(8.98, 52.42) * mm});
            skLineSegment(sketch, "E606.2.2.2", {"start": v(15.79, 54.81) * mm, "end": v(13.65, 49.1) * mm});
            skLineSegment(sketch, "E606.2.2.3", {"start": v(17.87, 49.1) * mm, "end": v(11.3, 42.24) * mm});
            skLineSegment(sketch, "E606.2.2.4", {"start": v(10.75, 50.62) * mm, "end": v(15.79, 54.81) * mm});
            skLineSegment(sketch, "E606.2.2.5", {"start": v(8.25, 51.47) * mm, "end": v(3.28, 46.07) * mm});
            skLineSegment(sketch, "E606.2.2.6", {"start": v(1.04, 52.91) * mm, "end": v(7.57, 59.23) * mm});
            skLineSegment(sketch, "E606.2.2.7", {"start": v(10.66, 46.25) * mm, "end": v(4.98, 44.63) * mm});
            skLineSegment(sketch, "E606.2.2.8", {"start": v(3.28, 46.07) * mm, "end": v(4.9, 52.77) * mm});
            skLineSegment(sketch, "E606.2.2.9", {"start": v(7.57, 55.44) * mm, "end": v(13.54, 56.92) * mm});
            skLineSegment(sketch, "E606.2.2.10", {"start": v(13.65, 49.1) * mm, "end": v(17.87, 49.1) * mm});
            skLineSegment(sketch, "E606.2.2.11", {"start": v(4.9, 52.77) * mm, "end": v(1.04, 52.91) * mm});
            skLineSegment(sketch, "E606.2.2.12", {"start": v(11.3, 42.24) * mm, "end": v(10.66, 46.25) * mm});
            skLineSegment(sketch, "E606.2.2.13", {"start": v(8.98, 52.42) * mm, "end": v(10.75, 50.62) * mm});
            skLineSegment(sketch, "E606.2.2.14", {"start": v(7.57, 59.23) * mm, "end": v(7.57, 55.44) * mm});
            skLineSegment(sketch, "E606.2.2.15", {"start": v(9.89, 49.97) * mm, "end": v(8.25, 51.47) * mm});
            skLineSegment(sketch, "E606.2.3.0", {"start": v(4.98, 25.07) * mm, "end": v(9.89, 30.4) * mm});
            skLineSegment(sketch, "E606.2.3.1", {"start": v(13.54, 37.36) * mm, "end": v(8.98, 32.87) * mm});
            skLineSegment(sketch, "E606.2.3.2", {"start": v(15.79, 35.25) * mm, "end": v(13.65, 29.54) * mm});
            skLineSegment(sketch, "E606.2.3.3", {"start": v(17.87, 29.54) * mm, "end": v(11.3, 22.69) * mm});
            skLineSegment(sketch, "E606.2.3.4", {"start": v(10.75, 31.06) * mm, "end": v(15.79, 35.25) * mm});
            skLineSegment(sketch, "E606.2.3.5", {"start": v(8.25, 31.92) * mm, "end": v(3.28, 26.52) * mm});
            skLineSegment(sketch, "E606.2.3.6", {"start": v(1.04, 33.36) * mm, "end": v(7.57, 39.67) * mm});
            skLineSegment(sketch, "E606.2.3.7", {"start": v(10.66, 26.69) * mm, "end": v(4.98, 25.07) * mm});
            skLineSegment(sketch, "E606.2.3.8", {"start": v(3.28, 26.52) * mm, "end": v(4.9, 33.22) * mm});
            skLineSegment(sketch, "E606.2.3.9", {"start": v(7.57, 35.88) * mm, "end": v(13.54, 37.36) * mm});
            skLineSegment(sketch, "E606.2.3.10", {"start": v(13.65, 29.54) * mm, "end": v(17.87, 29.54) * mm});
            skLineSegment(sketch, "E606.2.3.11", {"start": v(4.9, 33.22) * mm, "end": v(1.04, 33.36) * mm});
            skLineSegment(sketch, "E606.2.3.12", {"start": v(11.3, 22.69) * mm, "end": v(10.66, 26.69) * mm});
            skLineSegment(sketch, "E606.2.3.13", {"start": v(8.98, 32.87) * mm, "end": v(10.75, 31.06) * mm});
            skLineSegment(sketch, "E606.2.3.14", {"start": v(7.57, 39.67) * mm, "end": v(7.57, 35.88) * mm});
            skLineSegment(sketch, "E606.2.3.15", {"start": v(9.89, 30.4) * mm, "end": v(8.25, 31.92) * mm});
            skLineSegment(sketch, "E606.direction1", {"start": v(-34.82, 85.19) * mm, "end": v(-15.77, 85.19) * mm, "construction": true});
            skLineSegment(sketch, "E606.direction2", {"start": v(-34.82, 85.19) * mm, "end": v(-34.82, 65.63) * mm, "construction": true});
            skLineSegment(sketch, "E607.0.3.0", {"start": v(24.03, 83.75) * mm, "end": v(28.94, 89.08) * mm});
            skLineSegment(sketch, "E607.3.3.0", {"start": v(32.6, 96.03) * mm, "end": v(28.03, 91.54) * mm});
            skLineSegment(sketch, "E607.6.3.0", {"start": v(34.84, 93.93) * mm, "end": v(32.7, 88.22) * mm});
            skLineSegment(sketch, "E607.9.3.0", {"start": v(36.92, 88.22) * mm, "end": v(30.34, 81.36) * mm});
            skLineSegment(sketch, "E607.12.3.0", {"start": v(29.8, 89.73) * mm, "end": v(34.84, 93.93) * mm});
            skLineSegment(sketch, "E607.15.3.0", {"start": v(27.3, 90.59) * mm, "end": v(22.33, 85.19) * mm});
            skLineSegment(sketch, "E607.18.3.0", {"start": v(20.1, 92.03) * mm, "end": v(26.62, 98.35) * mm});
            skLineSegment(sketch, "E607.21.3.0", {"start": v(29.71, 85.36) * mm, "end": v(24.03, 83.75) * mm});
            skLineSegment(sketch, "E607.24.3.0", {"start": v(22.33, 85.19) * mm, "end": v(23.96, 91.9) * mm});
            skLineSegment(sketch, "E607.27.3.0", {"start": v(26.62, 94.56) * mm, "end": v(32.6, 96.03) * mm});
            skLineSegment(sketch, "E607.30.3.0", {"start": v(32.7, 88.22) * mm, "end": v(36.92, 88.22) * mm});
            skLineSegment(sketch, "E607.33.3.0", {"start": v(23.96, 91.9) * mm, "end": v(20.1, 92.03) * mm});
            skLineSegment(sketch, "E607.36.3.0", {"start": v(30.34, 81.36) * mm, "end": v(29.71, 85.36) * mm});
            skLineSegment(sketch, "E607.39.3.0", {"start": v(28.03, 91.54) * mm, "end": v(29.8, 89.73) * mm});
            skLineSegment(sketch, "E607.42.3.0", {"start": v(26.62, 98.35) * mm, "end": v(26.62, 94.56) * mm});
            skLineSegment(sketch, "E607.45.3.0", {"start": v(28.94, 89.08) * mm, "end": v(27.3, 90.59) * mm});
            skLineSegment(sketch, "E607.0.3.1", {"start": v(24.03, 64.19) * mm, "end": v(28.94, 69.52) * mm});
            skLineSegment(sketch, "E607.3.3.1", {"start": v(32.6, 76.47) * mm, "end": v(28.03, 71.98) * mm});
            skLineSegment(sketch, "E607.6.3.1", {"start": v(34.84, 74.37) * mm, "end": v(32.7, 68.66) * mm});
            skLineSegment(sketch, "E607.9.3.1", {"start": v(36.92, 68.66) * mm, "end": v(30.34, 61.8) * mm});
            skLineSegment(sketch, "E607.12.3.1", {"start": v(29.8, 70.18) * mm, "end": v(34.84, 74.37) * mm});
            skLineSegment(sketch, "E607.15.3.1", {"start": v(27.3, 71.03) * mm, "end": v(22.33, 65.63) * mm});
            skLineSegment(sketch, "E607.18.3.1", {"start": v(20.1, 72.47) * mm, "end": v(26.62, 78.8) * mm});
            skLineSegment(sketch, "E607.21.3.1", {"start": v(29.71, 65.8) * mm, "end": v(24.03, 64.19) * mm});
            skLineSegment(sketch, "E607.24.3.1", {"start": v(22.33, 65.63) * mm, "end": v(23.96, 72.33) * mm});
            skLineSegment(sketch, "E607.27.3.1", {"start": v(26.62, 75) * mm, "end": v(32.6, 76.47) * mm});
            skLineSegment(sketch, "E607.30.3.1", {"start": v(32.7, 68.66) * mm, "end": v(36.92, 68.66) * mm});
            skLineSegment(sketch, "E607.33.3.1", {"start": v(23.96, 72.33) * mm, "end": v(20.1, 72.47) * mm});
            skLineSegment(sketch, "E607.36.3.1", {"start": v(30.34, 61.8) * mm, "end": v(29.71, 65.8) * mm});
            skLineSegment(sketch, "E607.39.3.1", {"start": v(28.03, 71.98) * mm, "end": v(29.8, 70.18) * mm});
            skLineSegment(sketch, "E607.42.3.1", {"start": v(26.62, 78.8) * mm, "end": v(26.62, 75) * mm});
            skLineSegment(sketch, "E607.45.3.1", {"start": v(28.94, 69.52) * mm, "end": v(27.3, 71.03) * mm});
            skLineSegment(sketch, "E607.0.3.2", {"start": v(24.03, 44.63) * mm, "end": v(28.94, 49.97) * mm});
            skLineSegment(sketch, "E607.3.3.2", {"start": v(32.6, 56.92) * mm, "end": v(28.03, 52.42) * mm});
            skLineSegment(sketch, "E607.6.3.2", {"start": v(34.84, 54.81) * mm, "end": v(32.7, 49.1) * mm});
            skLineSegment(sketch, "E607.9.3.2", {"start": v(36.92, 49.1) * mm, "end": v(30.34, 42.24) * mm});
            skLineSegment(sketch, "E607.12.3.2", {"start": v(29.8, 50.62) * mm, "end": v(34.84, 54.81) * mm});
            skLineSegment(sketch, "E607.15.3.2", {"start": v(27.3, 51.47) * mm, "end": v(22.33, 46.07) * mm});
            skLineSegment(sketch, "E607.18.3.2", {"start": v(20.1, 52.91) * mm, "end": v(26.62, 59.23) * mm});
            skLineSegment(sketch, "E607.21.3.2", {"start": v(29.71, 46.25) * mm, "end": v(24.03, 44.63) * mm});
            skLineSegment(sketch, "E607.24.3.2", {"start": v(22.33, 46.07) * mm, "end": v(23.96, 52.77) * mm});
            skLineSegment(sketch, "E607.27.3.2", {"start": v(26.62, 55.44) * mm, "end": v(32.6, 56.92) * mm});
            skLineSegment(sketch, "E607.30.3.2", {"start": v(32.7, 49.1) * mm, "end": v(36.92, 49.1) * mm});
            skLineSegment(sketch, "E607.33.3.2", {"start": v(23.96, 52.77) * mm, "end": v(20.1, 52.91) * mm});
            skLineSegment(sketch, "E607.36.3.2", {"start": v(30.34, 42.24) * mm, "end": v(29.71, 46.25) * mm});
            skLineSegment(sketch, "E607.39.3.2", {"start": v(28.03, 52.42) * mm, "end": v(29.8, 50.62) * mm});
            skLineSegment(sketch, "E607.42.3.2", {"start": v(26.62, 59.23) * mm, "end": v(26.62, 55.44) * mm});
            skLineSegment(sketch, "E607.45.3.2", {"start": v(28.94, 49.97) * mm, "end": v(27.3, 51.47) * mm});
            skLineSegment(sketch, "E607.0.3.3", {"start": v(24.03, 25.07) * mm, "end": v(28.94, 30.4) * mm});
            skLineSegment(sketch, "E607.3.3.3", {"start": v(32.6, 37.36) * mm, "end": v(28.03, 32.87) * mm});
            skLineSegment(sketch, "E607.6.3.3", {"start": v(34.84, 35.25) * mm, "end": v(32.7, 29.54) * mm});
            skLineSegment(sketch, "E607.9.3.3", {"start": v(36.92, 29.54) * mm, "end": v(30.34, 22.69) * mm});
            skLineSegment(sketch, "E607.12.3.3", {"start": v(29.8, 31.06) * mm, "end": v(34.84, 35.25) * mm});
            skLineSegment(sketch, "E607.15.3.3", {"start": v(27.3, 31.92) * mm, "end": v(22.33, 26.52) * mm});
            skLineSegment(sketch, "E607.18.3.3", {"start": v(20.1, 33.36) * mm, "end": v(26.62, 39.67) * mm});
            skLineSegment(sketch, "E607.21.3.3", {"start": v(29.71, 26.69) * mm, "end": v(24.03, 25.07) * mm});
            skLineSegment(sketch, "E607.24.3.3", {"start": v(22.33, 26.52) * mm, "end": v(23.96, 33.22) * mm});
            skLineSegment(sketch, "E607.27.3.3", {"start": v(26.62, 35.88) * mm, "end": v(32.6, 37.36) * mm});
            skLineSegment(sketch, "E607.30.3.3", {"start": v(32.7, 29.54) * mm, "end": v(36.92, 29.54) * mm});
            skLineSegment(sketch, "E607.33.3.3", {"start": v(23.96, 33.22) * mm, "end": v(20.1, 33.36) * mm});
            skLineSegment(sketch, "E607.36.3.3", {"start": v(30.34, 22.69) * mm, "end": v(29.71, 26.69) * mm});
            skLineSegment(sketch, "E607.39.3.3", {"start": v(28.03, 32.87) * mm, "end": v(29.8, 31.06) * mm});
            skLineSegment(sketch, "E607.42.3.3", {"start": v(26.62, 39.67) * mm, "end": v(26.62, 35.88) * mm});
            skLineSegment(sketch, "E607.45.3.3", {"start": v(28.94, 30.4) * mm, "end": v(27.3, 31.92) * mm});
            skLineSegment(sketch, "E608.0.0.4", {"start": v(-33.12, 5.51) * mm, "end": v(-28.21, 10.85) * mm});
            skLineSegment(sketch, "E608.3.0.4", {"start": v(-24.56, 17.8) * mm, "end": v(-29.12, 13.3) * mm});
            skLineSegment(sketch, "E608.6.0.4", {"start": v(-22.31, 15.7) * mm, "end": v(-24.45, 9.99) * mm});
            skLineSegment(sketch, "E608.9.0.4", {"start": v(-20.23, 9.99) * mm, "end": v(-26.8, 3.13) * mm});
            skLineSegment(sketch, "E608.12.0.4", {"start": v(-27.35, 11.5) * mm, "end": v(-22.31, 15.7) * mm});
            skLineSegment(sketch, "E608.15.0.4", {"start": v(-29.85, 12.36) * mm, "end": v(-34.82, 6.96) * mm});
            skLineSegment(sketch, "E608.18.0.4", {"start": v(-37.06, 13.8) * mm, "end": v(-30.53, 20.12) * mm});
            skLineSegment(sketch, "E608.21.0.4", {"start": v(-27.44, 7.13) * mm, "end": v(-33.12, 5.51) * mm});
            skLineSegment(sketch, "E608.24.0.4", {"start": v(-34.82, 6.96) * mm, "end": v(-33.2, 13.66) * mm});
            skLineSegment(sketch, "E608.27.0.4", {"start": v(-30.53, 16.33) * mm, "end": v(-24.56, 17.8) * mm});
            skLineSegment(sketch, "E608.30.0.4", {"start": v(-24.45, 9.99) * mm, "end": v(-20.23, 9.99) * mm});
            skLineSegment(sketch, "E608.33.0.4", {"start": v(-33.2, 13.66) * mm, "end": v(-37.06, 13.8) * mm});
            skLineSegment(sketch, "E608.36.0.4", {"start": v(-26.8, 3.13) * mm, "end": v(-27.44, 7.13) * mm});
            skLineSegment(sketch, "E608.39.0.4", {"start": v(-29.12, 13.3) * mm, "end": v(-27.35, 11.5) * mm});
            skLineSegment(sketch, "E608.42.0.4", {"start": v(-30.53, 20.12) * mm, "end": v(-30.53, 16.33) * mm});
            skLineSegment(sketch, "E608.45.0.4", {"start": v(-28.21, 10.85) * mm, "end": v(-29.85, 12.36) * mm});
            skLineSegment(sketch, "E608.0.1.4", {"start": v(-14.07, 5.51) * mm, "end": v(-9.16, 10.85) * mm});
            skLineSegment(sketch, "E608.3.1.4", {"start": v(-5.5, 17.8) * mm, "end": v(-10.07, 13.3) * mm});
            skLineSegment(sketch, "E608.6.1.4", {"start": v(-3.26, 15.7) * mm, "end": v(-5.4, 9.99) * mm});
            skLineSegment(sketch, "E608.9.1.4", {"start": v(-1.18, 9.99) * mm, "end": v(-7.76, 3.13) * mm});
            skLineSegment(sketch, "E608.12.1.4", {"start": v(-8.3, 11.5) * mm, "end": v(-3.26, 15.7) * mm});
            skLineSegment(sketch, "E608.15.1.4", {"start": v(-10.8, 12.36) * mm, "end": v(-15.77, 6.96) * mm});
            skLineSegment(sketch, "E608.18.1.4", {"start": v(-18, 13.8) * mm, "end": v(-11.48, 20.12) * mm});
            skLineSegment(sketch, "E608.21.1.4", {"start": v(-8.39, 7.13) * mm, "end": v(-14.07, 5.51) * mm});
            skLineSegment(sketch, "E608.24.1.4", {"start": v(-15.77, 6.96) * mm, "end": v(-14.14, 13.66) * mm});
            skLineSegment(sketch, "E608.27.1.4", {"start": v(-11.48, 16.33) * mm, "end": v(-5.5, 17.8) * mm});
            skLineSegment(sketch, "E608.30.1.4", {"start": v(-5.4, 9.99) * mm, "end": v(-1.18, 9.99) * mm});
            skLineSegment(sketch, "E608.33.1.4", {"start": v(-14.14, 13.66) * mm, "end": v(-18, 13.8) * mm});
            skLineSegment(sketch, "E608.36.1.4", {"start": v(-7.76, 3.13) * mm, "end": v(-8.39, 7.13) * mm});
            skLineSegment(sketch, "E608.39.1.4", {"start": v(-10.07, 13.3) * mm, "end": v(-8.3, 11.5) * mm});
            skLineSegment(sketch, "E608.42.1.4", {"start": v(-11.48, 20.12) * mm, "end": v(-11.48, 16.33) * mm});
            skLineSegment(sketch, "E608.45.1.4", {"start": v(-9.16, 10.85) * mm, "end": v(-10.8, 12.36) * mm});
            skLineSegment(sketch, "E608.0.2.4", {"start": v(4.98, 5.51) * mm, "end": v(9.89, 10.85) * mm});
            skLineSegment(sketch, "E608.3.2.4", {"start": v(13.54, 17.8) * mm, "end": v(8.98, 13.3) * mm});
            skLineSegment(sketch, "E608.6.2.4", {"start": v(15.79, 15.7) * mm, "end": v(13.65, 9.99) * mm});
            skLineSegment(sketch, "E608.9.2.4", {"start": v(17.87, 9.99) * mm, "end": v(11.3, 3.13) * mm});
            skLineSegment(sketch, "E608.12.2.4", {"start": v(10.75, 11.5) * mm, "end": v(15.79, 15.7) * mm});
            skLineSegment(sketch, "E608.15.2.4", {"start": v(8.25, 12.36) * mm, "end": v(3.28, 6.96) * mm});
            skLineSegment(sketch, "E608.18.2.4", {"start": v(1.04, 13.8) * mm, "end": v(7.57, 20.12) * mm});
            skLineSegment(sketch, "E608.21.2.4", {"start": v(10.66, 7.13) * mm, "end": v(4.98, 5.51) * mm});
            skLineSegment(sketch, "E608.24.2.4", {"start": v(3.28, 6.96) * mm, "end": v(4.9, 13.66) * mm});
            skLineSegment(sketch, "E608.27.2.4", {"start": v(7.57, 16.33) * mm, "end": v(13.54, 17.8) * mm});
            skLineSegment(sketch, "E608.30.2.4", {"start": v(13.65, 9.99) * mm, "end": v(17.87, 9.99) * mm});
            skLineSegment(sketch, "E608.33.2.4", {"start": v(4.9, 13.66) * mm, "end": v(1.04, 13.8) * mm});
            skLineSegment(sketch, "E608.36.2.4", {"start": v(11.3, 3.13) * mm, "end": v(10.66, 7.13) * mm});
            skLineSegment(sketch, "E608.39.2.4", {"start": v(8.98, 13.3) * mm, "end": v(10.75, 11.5) * mm});
            skLineSegment(sketch, "E608.42.2.4", {"start": v(7.57, 20.12) * mm, "end": v(7.57, 16.33) * mm});
            skLineSegment(sketch, "E608.45.2.4", {"start": v(9.89, 10.85) * mm, "end": v(8.25, 12.36) * mm});
            skLineSegment(sketch, "E608.0.3.4", {"start": v(24.03, 5.51) * mm, "end": v(28.94, 10.85) * mm});
            skLineSegment(sketch, "E608.3.3.4", {"start": v(32.6, 17.8) * mm, "end": v(28.03, 13.3) * mm});
            skLineSegment(sketch, "E608.6.3.4", {"start": v(34.84, 15.7) * mm, "end": v(32.7, 9.99) * mm});
            skLineSegment(sketch, "E608.9.3.4", {"start": v(36.92, 9.99) * mm, "end": v(30.34, 3.13) * mm});
            skLineSegment(sketch, "E608.12.3.4", {"start": v(29.8, 11.5) * mm, "end": v(34.84, 15.7) * mm});
            skLineSegment(sketch, "E608.15.3.4", {"start": v(27.3, 12.36) * mm, "end": v(22.33, 6.96) * mm});
            skLineSegment(sketch, "E608.18.3.4", {"start": v(20.1, 13.8) * mm, "end": v(26.62, 20.12) * mm});
            skLineSegment(sketch, "E608.21.3.4", {"start": v(29.71, 7.13) * mm, "end": v(24.03, 5.51) * mm});
            skLineSegment(sketch, "E608.24.3.4", {"start": v(22.33, 6.96) * mm, "end": v(23.96, 13.66) * mm});
            skLineSegment(sketch, "E608.27.3.4", {"start": v(26.62, 16.33) * mm, "end": v(32.6, 17.8) * mm});
            skLineSegment(sketch, "E608.30.3.4", {"start": v(32.7, 9.99) * mm, "end": v(36.92, 9.99) * mm});
            skLineSegment(sketch, "E608.33.3.4", {"start": v(23.96, 13.66) * mm, "end": v(20.1, 13.8) * mm});
            skLineSegment(sketch, "E608.36.3.4", {"start": v(30.34, 3.13) * mm, "end": v(29.71, 7.13) * mm});
            skLineSegment(sketch, "E608.39.3.4", {"start": v(28.03, 13.3) * mm, "end": v(29.8, 11.5) * mm});
            skLineSegment(sketch, "E608.42.3.4", {"start": v(26.62, 20.12) * mm, "end": v(26.62, 16.33) * mm});
            skLineSegment(sketch, "E608.45.3.4", {"start": v(28.94, 10.85) * mm, "end": v(27.3, 12.36) * mm});
            skSolve(sketch);
        }
        {
            var Q0;
            Q0=qSketchRegion(id+"F12",true);
            extrude(context, id + "F13", {"entities" : qUnion([Q0]), "operationType" : NewBodyOperationType.REMOVE, "oppositeDirection" : true, "depth" : 228.6 * mm, "offsetDistance" : 25.4 * mm});
        }
        {
            var Q0;
            Q0=makeQuery(id+"F4.opExtrude","SWEPT_FACE",FACE,{"disambiguationData":[OSD([sQuery(id+"F3.wireOp",EDGE,"E5.left")])]});
            var sketch = newSketch(context, id + "F14", { "sketchPlane" : qUnion([Q0])});
            skLineSegment(sketch, "E609", {"start": v(0, 111.13) * mm, "end": v(0, 101.6) * mm, "construction": true});
            skLineSegment(sketch, "E610", {"start": v(-38.1, 106.36) * mm, "end": v(38.1, 106.36) * mm, "construction": true});
            skCircle(sketch, "E611", {"center": v(0, 106.36) * mm, "radius": 1.59 * mm});
            skCircle(sketch, "E612", {"center": v(-16.51, 106.36) * mm, "radius": 1.59 * mm});
            skCircle(sketch, "E613", {"center": v(16.5, 106.36) * mm, "radius": 1.59 * mm});
            skCircle(sketch, "E614", {"center": v(-33.02, 106.36) * mm, "radius": 1.59 * mm});
            skCircle(sketch, "E615", {"center": v(33.02, 106.36) * mm, "radius": 1.59 * mm});
            skLineSegment(sketch, "E616", {"start": v(-38.1, 0) * mm, "end": v(-38.1, 101.6) * mm, "construction": true});
            skLineSegment(sketch, "E617", {"start": v(-38.1, 101.6) * mm, "end": v(-38.1, 0) * mm, "construction": true});
            skLineSegment(sketch, "E618", {"start": v(38.1, 101.6) * mm, "end": v(38.1, 0) * mm, "construction": true});
            skLineSegment(sketch, "E619", {"start": v(38.1, 0) * mm, "end": v(38.1, 101.6) * mm, "construction": true});
            skLineSegment(sketch, "E620", {"start": v(-38.1, 50.8) * mm, "end": v(38.1, 50.8) * mm, "construction": true});
            skCircle(sketch, "E621.MirrorC", {"center": v(33.02, -4.76) * mm, "radius": 1.59 * mm});
            skCircle(sketch, "E622.MirrorC", {"center": v(16.5, -4.76) * mm, "radius": 1.59 * mm});
            skCircle(sketch, "E623.MirrorC", {"center": v(0, -4.76) * mm, "radius": 1.59 * mm});
            skCircle(sketch, "E624.MirrorC", {"center": v(-16.51, -4.76) * mm, "radius": 1.59 * mm});
            skCircle(sketch, "E625.MirrorC", {"center": v(-33.02, -4.76) * mm, "radius": 1.59 * mm});
            skSolve(sketch);
        }
        {
            var Q0;
            Q0=qSketchRegion(id+"F14",true);
            extrude(context, id + "F15", {"entities" : qUnion([Q0]), "operationType" : NewBodyOperationType.REMOVE, "oppositeDirection" : true, "depth" : 228.6 * mm, "offsetDistance" : 25.4 * mm});
        }
        {
            var Q0;
            Q0=makeQuery(id+"F1.opExtrude","SWEPT_FACE",FACE,{"disambiguationData":[OSD([sQuery(id+"F0.wireOp",EDGE,"E2.filletArc")])]});
            cPlane(context, id + "F16", {"entities" : qUnion([Q0]), "cplaneType" : CPlaneType.LINE_ANGLE, "offset" : 25.4 * mm, "angle" : 45 * degree, "width" : 152.4 * mm, "height" : 152.4 * mm});
        }
        {
            var Q0;
            Q0=qCreatedBy(id+"F16.planeOp",FACE);
            var sketch = newSketch(context, id + "F17", { "sketchPlane" : qUnion([Q0])});
            skLineSegment(sketch, "E626", {"start": v(-44.94, 0) * mm, "end": v(-26.56, 0) * mm});
            skPoint(sketch, "E627", {"position": v(-35.75, 0) * mm});
            skLineSegment(sketch, "E628", {"start": v(-35.75, 0) * mm, "end": v(-35.75, -9.46) * mm, "construction": true});
            skCircle(sketch, "E629", {"center": v(-35.75, -4.73) * mm, "radius": 1.59 * mm});
            skPoint(sketch, "E630", {"position": v(-35.92, 101.7) * mm});
            skLineSegment(sketch, "E631", {"start": v(-35.92, 101.7) * mm, "end": v(-35.92, 111.13) * mm, "construction": true});
            skCircle(sketch, "E632", {"center": v(-35.92, 106.4) * mm, "radius": 1.59 * mm});
            skSolve(sketch);
        }
        {
            var Q0;
            Q0=qSketchRegion(id+"F17",true);
            extrude(context, id + "F18", {"entities" : qUnion([Q0]), "operationType" : NewBodyOperationType.REMOVE, "oppositeDirection" : true, "depth" : 50.8 * mm, "offsetDistance" : 25.4 * mm});
        }
        {
            var Q0;
            Q0=makeQuery(id+"F1.opExtrude","CAP_EDGE",EDGE,{"disambiguationData":[OSD([sQuery(id+"F0.wireOp",EDGE,"E1.filletArc")])],"isStart":false});
            cPoint(context, id + "F19", {"entities" : qUnion([Q0]), "parameter" : 0.5});
        }
        {
            var Q0;
            Q0=makeQuery(id+"F1.opExtrude","SWEPT_FACE",FACE,{"disambiguationData":[OSD([sQuery(id+"F0.wireOp",EDGE,"E1.filletArc")])]});
            var Q1;
            Q1=qCreatedBy(id+"F19",VERTEX);
            cPlane(context, id + "F20", {"entities" : qUnion([Q0, Q1]), "cplaneType" : CPlaneType.LINE_ANGLE, "offset" : 25.4 * mm, "angle" : 90 * degree, "oppositeDirection" : true, "width" : 152.4 * mm, "height" : 152.4 * mm});
        }
        {
            var Q0;
            Q0=qCreatedBy(id+"F20.planeOp",FACE);
            var sketch = newSketch(context, id + "F21", { "sketchPlane" : qUnion([Q0])});
            skLineSegment(sketch, "E633", {"start": v(-44.95, 0) * mm, "end": v(-26.97, 0) * mm, "construction": true});
            skLineSegment(sketch, "E634", {"start": v(-35.96, 0) * mm, "end": v(-35.96, -9.52) * mm, "construction": true});
            skCircle(sketch, "E635", {"center": v(-35.96, -4.76) * mm, "radius": 1.59 * mm});
            skLineSegment(sketch, "E636", {"start": v(-35.96, 111.2) * mm, "end": v(-35.96, 101.65) * mm, "construction": true});
            skCircle(sketch, "E637", {"center": v(-35.96, 106.42) * mm, "radius": 1.59 * mm});
            skSolve(sketch);
        }
        {
            var Q0;
            Q0=qSketchRegion(id+"F21",true);
            extrude(context, id + "F22", {"entities" : qUnion([Q0]), "operationType" : NewBodyOperationType.REMOVE, "depth" : 50.8 * mm, "offsetDistance" : 25.4 * mm});
        }
        {
            var Q0;
            Q0=qCreatedBy(id+"F16.planeOp",FACE);
            cPlane(context, id + "F23", {"entities" : qUnion([Q0]), "cplaneType" : CPlaneType.OFFSET, "offset" : 177.8 * mm, "width" : 152.4 * mm, "height" : 152.4 * mm});
        }
        {
            var Q0;
            Q0=qCreatedBy(id+"F23.planeOp",FACE);
            var sketch = newSketch(context, id + "F24", { "sketchPlane" : qUnion([Q0])});
            skLineSegment(sketch, "E638", {"start": v(26.95, 0) * mm, "end": v(44.9, 0) * mm, "construction": true});
            skLineSegment(sketch, "E639", {"start": v(35.93, 0) * mm, "end": v(35.93, -9.44) * mm, "construction": true});
            skCircle(sketch, "E640", {"center": v(35.93, -4.72) * mm, "radius": 1.59 * mm});
            skLineSegment(sketch, "E641", {"start": v(35.93, 111.22) * mm, "end": v(35.93, 101.61) * mm, "construction": true});
            skCircle(sketch, "E642", {"center": v(35.93, 106.42) * mm, "radius": 1.59 * mm});
            skSolve(sketch);
        }
        {
            var Q0;
            Q0=qSketchRegion(id+"F24",true);
            extrude(context, id + "F25", {"entities" : qUnion([Q0]), "operationType" : NewBodyOperationType.REMOVE, "depth" : 76.2 * mm, "offsetDistance" : 25.4 * mm});
        }
        {
            var Q0;
            Q0=qCreatedBy(id+"F20.planeOp",FACE);
            cPlane(context, id + "F26", {"entities" : qUnion([Q0]), "cplaneType" : CPlaneType.OFFSET, "offset" : 177.8 * mm, "oppositeDirection" : true, "width" : 152.4 * mm, "height" : 152.4 * mm});
        }
        {
            var Q0;
            Q0=qCreatedBy(id+"F26.planeOp",FACE);
            var sketch = newSketch(context, id + "F27", { "sketchPlane" : qUnion([Q0])});
            skLineSegment(sketch, "E643", {"start": v(26.9, 101.67) * mm, "end": v(44.94, 101.67) * mm, "construction": true});
            skLineSegment(sketch, "E644", {"start": v(35.92, 101.67) * mm, "end": v(35.92, 111.22) * mm, "construction": true});
            skCircle(sketch, "E645", {"center": v(35.92, 106.44) * mm, "radius": 1.59 * mm});
            skLineSegment(sketch, "E646", {"start": v(35.92, 0) * mm, "end": v(35.92, -9.55) * mm, "construction": true});
            skCircle(sketch, "E647", {"center": v(35.92, -4.77) * mm, "radius": 1.59 * mm});
            skSolve(sketch);
        }
        {
            var Q0;
            Q0=qSketchRegion(id+"F27",true);
            extrude(context, id + "F28", {"entities" : qUnion([Q0]), "operationType" : NewBodyOperationType.REMOVE, "oppositeDirection" : true, "depth" : 76.2 * mm, "offsetDistance" : 25.4 * mm});
        }
    });
